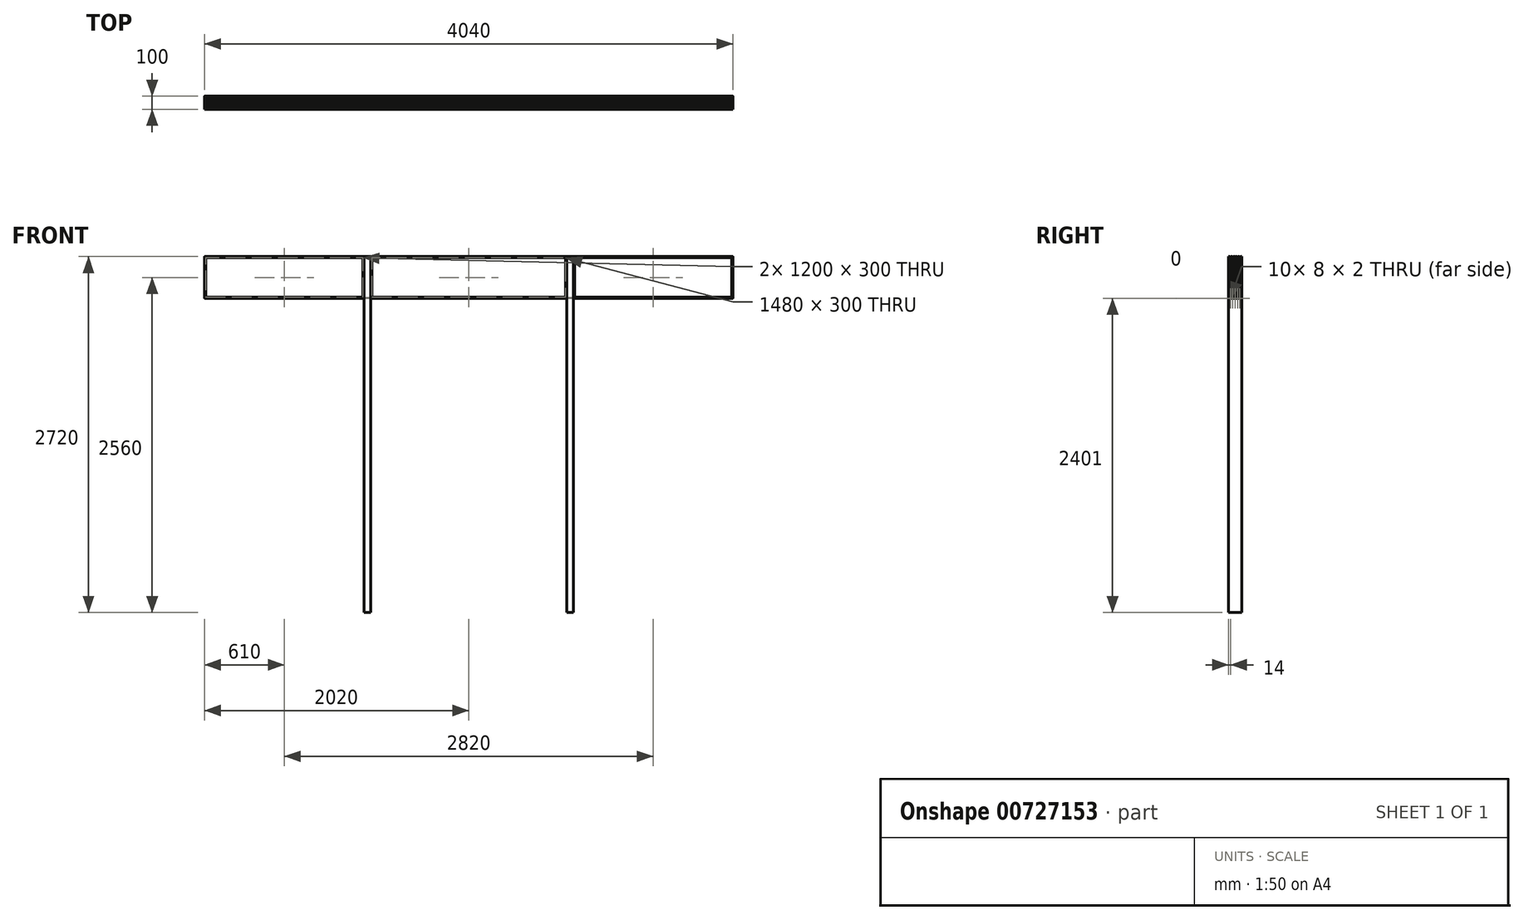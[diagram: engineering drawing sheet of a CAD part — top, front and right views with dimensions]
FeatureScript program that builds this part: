
annotation { "Feature Type Name" : "Feature", "Feature Type Description" : "" }
export const myFeature = defineFeature(function(context is Context, id is Id, definition is map)
    precondition{}
    {
        {
            var Q0;
            Q0=qCreatedBy(makeId("Front.planeOp"),FACE);
            var sketch = newSketch(context, id + "F0", { "sketchPlane" : qUnion([Q0])});
            skLineSegment(sketch, "E0.bottom", {"start": v(-800, 0) * mm, "end": v(-750, 0) * mm});
            skLineSegment(sketch, "E0.top", {"start": v(-800, -2720) * mm, "end": v(-750, -2720) * mm});
            skLineSegment(sketch, "E0.left", {"start": v(-800, 0) * mm, "end": v(-800, -2720) * mm});
            skLineSegment(sketch, "E0.right", {"start": v(-750, 0) * mm, "end": v(-750, -2720) * mm});
            skLineSegment(sketch, "E1.MirrorCS", {"start": v(800, -2720) * mm, "end": v(750, -2720) * mm});
            skLineSegment(sketch, "E2.MirrorCS", {"start": v(750, 0) * mm, "end": v(750, -2720) * mm});
            skLineSegment(sketch, "E3.MirrorCS", {"start": v(800, 0) * mm, "end": v(750, 0) * mm});
            skLineSegment(sketch, "E4.MirrorCS", {"start": v(800, 0) * mm, "end": v(800, -2720) * mm});
            skSolve(sketch);
        }
        {
            var Q0;
            Q0=qSketchRegion(id+"F0",true);
            extrude(context, id + "F1", {"entities" : qUnion([Q0]), "depth" : 100 * mm, "offsetDistance" : 25 * mm});
        }
        {
            var Q0;
            Q0=makeQuery(id+"F1.opExtrude","SWEPT_FACE",FACE,{"disambiguationData":[OSD([sQuery(id+"F0.wireOp",EDGE,"E0.bottom")])]});
            var sketch = newSketch(context, id + "F2", { "sketchPlane" : qUnion([Q0])});
            skLineSegment(sketch, "E5.bottom", {"start": v(-800, -100) * mm, "end": v(-2020, -100) * mm});
            skLineSegment(sketch, "E5.top", {"start": v(-800, 0) * mm, "end": v(-2020, 0) * mm});
            skLineSegment(sketch, "E5.left", {"start": v(-800, -100) * mm, "end": v(-800, 0) * mm});
            skLineSegment(sketch, "E5.right", {"start": v(-2020, -100) * mm, "end": v(-2020, 0) * mm});
            skLineSegment(sketch, "E6.bottom", {"start": v(-750, -100) * mm, "end": v(750, -100) * mm});
            skLineSegment(sketch, "E6.top", {"start": v(-750, 0) * mm, "end": v(750, 0) * mm});
            skLineSegment(sketch, "E6.left", {"start": v(-750, -100) * mm, "end": v(-750, 0) * mm});
            skLineSegment(sketch, "E6.right", {"start": v(750, -100) * mm, "end": v(750, 0) * mm});
            skLineSegment(sketch, "E7.bottom", {"start": v(800, -100) * mm, "end": v(2020, -100) * mm});
            skLineSegment(sketch, "E7.top", {"start": v(800, 0) * mm, "end": v(2020, 0) * mm});
            skLineSegment(sketch, "E7.left", {"start": v(800, -100) * mm, "end": v(800, 0) * mm});
            skLineSegment(sketch, "E7.right", {"start": v(2020, -100) * mm, "end": v(2020, 0) * mm});
            skSolve(sketch);
        }
        {
            var Q0;
            Q0=qSketchRegion(id+"F2",true);
            extrude(context, id + "F3", {"entities" : qUnion([Q0]), "oppositeDirection" : true, "depth" : 320 * mm, "offsetDistance" : 25 * mm});
        }
        {
            var Q0;
            Q0=makeQuery(id+"F3.opExtrude","SWEPT_FACE",FACE,{"disambiguationData":[OSD([sQuery(id+"F2.wireOp",EDGE,"E6.bottom")])]});
            var sketch = newSketch(context, id + "F4", { "sketchPlane" : qUnion([Q0])});
            skLineSegment(sketch, "E8.0", {"start": v(-810, -10) * mm, "end": v(-2010, -10) * mm});
            skLineSegment(sketch, "E8.1", {"start": v(-810, -310) * mm, "end": v(-810, -10) * mm});
            skLineSegment(sketch, "E8.2", {"start": v(-2010, -310) * mm, "end": v(-810, -310) * mm});
            skLineSegment(sketch, "E8.3", {"start": v(-2010, -10) * mm, "end": v(-2010, -310) * mm});
            skLineSegment(sketch, "E9.0", {"start": v(740, -10) * mm, "end": v(-740, -10) * mm});
            skLineSegment(sketch, "E9.1", {"start": v(740, -310) * mm, "end": v(740, -10) * mm});
            skLineSegment(sketch, "E9.2", {"start": v(-740, -310) * mm, "end": v(740, -310) * mm});
            skLineSegment(sketch, "E9.3", {"start": v(-740, -10) * mm, "end": v(-740, -310) * mm});
            skLineSegment(sketch, "E10.0", {"start": v(2010, -10) * mm, "end": v(810, -10) * mm});
            skLineSegment(sketch, "E10.1", {"start": v(2010, -310) * mm, "end": v(2010, -10) * mm});
            skLineSegment(sketch, "E10.2", {"start": v(810, -310) * mm, "end": v(2010, -310) * mm});
            skLineSegment(sketch, "E10.3", {"start": v(810, -10) * mm, "end": v(810, -310) * mm});
            skSolve(sketch);
        }
        {
            var Q0;
            Q0=qSketchRegion(id+"F4",true);
            extrude(context, id + "F5", {"entities" : qUnion([Q0]), "operationType" : NewBodyOperationType.REMOVE, "endBound" : BoundingType.THROUGH_ALL, "oppositeDirection" : true, "depth" : 25 * mm, "offsetDistance" : 25 * mm});
        }
        {
            var Q0;
            Q0=makeQuery(id+"F3.opExtrude","SWEPT_FACE",FACE,{"disambiguationData":[OSD([sQuery(id+"F2.wireOp",EDGE,"E5.right")])]});
            var sketch = newSketch(context, id + "F6", { "sketchPlane" : qUnion([Q0])});
            skLineSegment(sketch, "E11", {"start": v(10, 0) * mm, "end": v(10, -2) * mm});
            skLineSegment(sketch, "E12", {"start": v(10, -2) * mm, "end": v(18, -2) * mm});
            skLineSegment(sketch, "E13", {"start": v(18, -2) * mm, "end": v(18, 0) * mm});
            skLineSegment(sketch, "E14.1.0.0", {"start": v(36, -2) * mm, "end": v(36, 0) * mm});
            skLineSegment(sketch, "E14.1.0.1", {"start": v(28, -2) * mm, "end": v(36, -2) * mm});
            skLineSegment(sketch, "E14.1.0.2", {"start": v(28, 0) * mm, "end": v(28, -2) * mm});
            skLineSegment(sketch, "E14.2.0.0", {"start": v(54, -2) * mm, "end": v(54, 0) * mm});
            skLineSegment(sketch, "E14.2.0.1", {"start": v(46, -2) * mm, "end": v(54, -2) * mm});
            skLineSegment(sketch, "E14.2.0.2", {"start": v(46, 0) * mm, "end": v(46, -2) * mm});
            skLineSegment(sketch, "E14.3.0.0", {"start": v(72, -2) * mm, "end": v(72, 0) * mm});
            skLineSegment(sketch, "E14.3.0.1", {"start": v(64, -2) * mm, "end": v(72, -2) * mm});
            skLineSegment(sketch, "E14.3.0.2", {"start": v(64, 0) * mm, "end": v(64, -2) * mm});
            skLineSegment(sketch, "E14.4.0.0", {"start": v(90, -2) * mm, "end": v(90, 0) * mm});
            skLineSegment(sketch, "E14.4.0.1", {"start": v(82, -2) * mm, "end": v(90, -2) * mm});
            skLineSegment(sketch, "E14.4.0.2", {"start": v(82, 0) * mm, "end": v(82, -2) * mm});
            skLineSegment(sketch, "E14.direction1", {"start": v(10, -2) * mm, "end": v(28, -2) * mm, "construction": true});
            skLineSegment(sketch, "E15", {"start": v(10, 0) * mm, "end": v(18, 0) * mm});
            skLineSegment(sketch, "E16", {"start": v(28, 0) * mm, "end": v(36, 0) * mm});
            skLineSegment(sketch, "E17", {"start": v(46, 0) * mm, "end": v(54, 0) * mm});
            skLineSegment(sketch, "E18", {"start": v(64, 0) * mm, "end": v(72, 0) * mm});
            skLineSegment(sketch, "E19", {"start": v(82, 0) * mm, "end": v(90, 0) * mm});
            skLineSegment(sketch, "E20", {"start": v(100, -160) * mm, "end": v(0, -160) * mm, "construction": true});
            skLineSegment(sketch, "E21.MirrorCS", {"start": v(90, -318) * mm, "end": v(90, -320) * mm});
            skLineSegment(sketch, "E22.MirrorCS", {"start": v(64, -320) * mm, "end": v(64, -318) * mm});
            skLineSegment(sketch, "E23.MirrorCS", {"start": v(10, -320) * mm, "end": v(10, -318) * mm});
            skLineSegment(sketch, "E24.MirrorCS", {"start": v(18, -318) * mm, "end": v(18, -320) * mm});
            skLineSegment(sketch, "E25.MirrorCS", {"start": v(36, -318) * mm, "end": v(36, -320) * mm});
            skLineSegment(sketch, "E26.MirrorCS", {"start": v(28, -320) * mm, "end": v(28, -318) * mm});
            skLineSegment(sketch, "E27.MirrorCS", {"start": v(54, -318) * mm, "end": v(54, -320) * mm});
            skLineSegment(sketch, "E28.MirrorCS", {"start": v(46, -320) * mm, "end": v(46, -318) * mm});
            skLineSegment(sketch, "E29.MirrorCS", {"start": v(72, -318) * mm, "end": v(72, -320) * mm});
            skLineSegment(sketch, "E30.MirrorCS", {"start": v(82, -320) * mm, "end": v(82, -318) * mm});
            skLineSegment(sketch, "E31.MirrorCS", {"start": v(10, -320) * mm, "end": v(18, -320) * mm});
            skLineSegment(sketch, "E32.MirrorCS", {"start": v(10, -318) * mm, "end": v(18, -318) * mm});
            skLineSegment(sketch, "E33.MirrorCS", {"start": v(64, -318) * mm, "end": v(72, -318) * mm});
            skLineSegment(sketch, "E34.MirrorCS", {"start": v(64, -320) * mm, "end": v(72, -320) * mm});
            skLineSegment(sketch, "E35.MirrorCS", {"start": v(82, -320) * mm, "end": v(90, -320) * mm});
            skLineSegment(sketch, "E36.MirrorCS", {"start": v(28, -320) * mm, "end": v(36, -320) * mm});
            skLineSegment(sketch, "E37.MirrorCS", {"start": v(82, -318) * mm, "end": v(90, -318) * mm});
            skLineSegment(sketch, "E38.MirrorCS", {"start": v(10, -318) * mm, "end": v(28, -318) * mm, "construction": true});
            skLineSegment(sketch, "E39.MirrorCS", {"start": v(46, -320) * mm, "end": v(54, -320) * mm});
            skLineSegment(sketch, "E40.MirrorCS", {"start": v(28, -318) * mm, "end": v(36, -318) * mm});
            skLineSegment(sketch, "E41.MirrorCS", {"start": v(46, -318) * mm, "end": v(54, -318) * mm});
            skSolve(sketch);
        }
        {
            var Q0;
            Q0=qSketchRegion(id+"F6",true);
            extrude(context, id + "F7", {"entities" : qUnion([Q0]), "operationType" : NewBodyOperationType.REMOVE, "endBound" : BoundingType.THROUGH_ALL, "oppositeDirection" : true, "depth" : 25 * mm, "offsetDistance" : 25 * mm});
        }
        {
            var Q0;
            {var subQ0=sQuery(id+"F2.wireOp",EDGE,"E5.top");var subQ1=sQuery(id+"F2.wireOp",EDGE,"E5.left");var subQ2=sQuery(id+"F2.wireOp",EDGE,"E5.right");Q0=makeQuery(id+"F7.boolean.opBoolean","SPLIT",FACE,{"disambiguationData":[TD([makeQuery(id+"F3.opExtrude","SWEPT_FACE",FACE,{"disambiguationData":[OSD([subQ0])]})])],"derivedFrom":makeQuery(id+"F3.opExtrude","CAP_FACE",FACE,{"disambiguationData":[OSD([sQuery(id+"F2.wireOp",EDGE,"E5.bottom"),subQ0,subQ1,subQ2])],"isStart":true})});}
            var sketch = newSketch(context, id + "F8", { "sketchPlane" : qUnion([Q0])});
            skLineSegment(sketch, "E42.bottom", {"start": v(-2018, -90) * mm, "end": v(-2020, -90) * mm});
            skLineSegment(sketch, "E42.top", {"start": v(-2018, -82) * mm, "end": v(-2020, -82) * mm});
            skLineSegment(sketch, "E42.left", {"start": v(-2018, -90) * mm, "end": v(-2018, -82) * mm});
            skLineSegment(sketch, "E42.right", {"start": v(-2020, -90) * mm, "end": v(-2020, -82) * mm});
            skLineSegment(sketch, "E43.0.1.0", {"start": v(-2018, -64) * mm, "end": v(-2020, -64) * mm});
            skLineSegment(sketch, "E43.0.1.1", {"start": v(-2018, -72) * mm, "end": v(-2020, -72) * mm});
            skLineSegment(sketch, "E43.0.1.2", {"start": v(-2020, -72) * mm, "end": v(-2020, -64) * mm});
            skLineSegment(sketch, "E43.0.1.3", {"start": v(-2018, -72) * mm, "end": v(-2018, -64) * mm});
            skLineSegment(sketch, "E43.0.2.0", {"start": v(-2018, -46) * mm, "end": v(-2020, -46) * mm});
            skLineSegment(sketch, "E43.0.2.1", {"start": v(-2018, -54) * mm, "end": v(-2020, -54) * mm});
            skLineSegment(sketch, "E43.0.2.2", {"start": v(-2020, -54) * mm, "end": v(-2020, -46) * mm});
            skLineSegment(sketch, "E43.0.2.3", {"start": v(-2018, -54) * mm, "end": v(-2018, -46) * mm});
            skLineSegment(sketch, "E43.0.3.0", {"start": v(-2018, -28) * mm, "end": v(-2020, -28) * mm});
            skLineSegment(sketch, "E43.0.3.1", {"start": v(-2018, -36) * mm, "end": v(-2020, -36) * mm});
            skLineSegment(sketch, "E43.0.3.2", {"start": v(-2020, -36) * mm, "end": v(-2020, -28) * mm});
            skLineSegment(sketch, "E43.0.3.3", {"start": v(-2018, -36) * mm, "end": v(-2018, -28) * mm});
            skLineSegment(sketch, "E43.0.4.0", {"start": v(-2018, -10) * mm, "end": v(-2020, -10) * mm});
            skLineSegment(sketch, "E43.0.4.1", {"start": v(-2018, -18) * mm, "end": v(-2020, -18) * mm});
            skLineSegment(sketch, "E43.0.4.2", {"start": v(-2020, -18) * mm, "end": v(-2020, -10) * mm});
            skLineSegment(sketch, "E43.0.4.3", {"start": v(-2018, -18) * mm, "end": v(-2018, -10) * mm});
            skLineSegment(sketch, "E43.direction1", {"start": v(-2770, -90) * mm, "end": v(-2020, -90) * mm, "construction": true});
            skLineSegment(sketch, "E43.direction2", {"start": v(-2020, -90) * mm, "end": v(-2020, -72) * mm, "construction": true});
            skPoint(sketch, "E44.0", {"position": v(0, -10) * mm});
            skLineSegment(sketch, "E45.MirrorCS", {"start": v(2018, -64) * mm, "end": v(2020, -64) * mm});
            skLineSegment(sketch, "E46.MirrorCS", {"start": v(2018, -36) * mm, "end": v(2020, -36) * mm});
            skLineSegment(sketch, "E47.MirrorCS", {"start": v(2018, -90) * mm, "end": v(2020, -90) * mm});
            skLineSegment(sketch, "E48.MirrorCS", {"start": v(2018, -82) * mm, "end": v(2020, -82) * mm});
            skLineSegment(sketch, "E49.MirrorCS", {"start": v(2018, -72) * mm, "end": v(2020, -72) * mm});
            skLineSegment(sketch, "E50.MirrorCS", {"start": v(2018, -46) * mm, "end": v(2020, -46) * mm});
            skLineSegment(sketch, "E51.MirrorCS", {"start": v(2018, -54) * mm, "end": v(2020, -54) * mm});
            skLineSegment(sketch, "E52.MirrorCS", {"start": v(2020, -36) * mm, "end": v(2020, -28) * mm});
            skLineSegment(sketch, "E53.MirrorCS", {"start": v(2018, -90) * mm, "end": v(2018, -82) * mm});
            skLineSegment(sketch, "E54.MirrorCS", {"start": v(2020, -72) * mm, "end": v(2020, -64) * mm});
            skLineSegment(sketch, "E55.MirrorCS", {"start": v(2020, -54) * mm, "end": v(2020, -46) * mm});
            skLineSegment(sketch, "E56.MirrorCS", {"start": v(2018, -36) * mm, "end": v(2018, -28) * mm});
            skLineSegment(sketch, "E57.MirrorCS", {"start": v(2020, -90) * mm, "end": v(2020, -82) * mm});
            skLineSegment(sketch, "E58.MirrorCS", {"start": v(2018, -72) * mm, "end": v(2018, -64) * mm});
            skLineSegment(sketch, "E59.MirrorCS", {"start": v(2018, -54) * mm, "end": v(2018, -46) * mm});
            skLineSegment(sketch, "E60.MirrorCS", {"start": v(2018, -28) * mm, "end": v(2020, -28) * mm});
            skLineSegment(sketch, "E61.MirrorCS", {"start": v(2020, -90) * mm, "end": v(2020, -72) * mm, "construction": true});
            skLineSegment(sketch, "E62.MirrorCS", {"start": v(2770, -90) * mm, "end": v(2020, -90) * mm, "construction": true});
            skLineSegment(sketch, "E63.MirrorCS", {"start": v(2018, -18) * mm, "end": v(2020, -18) * mm});
            skLineSegment(sketch, "E64.MirrorCS", {"start": v(2020, -18) * mm, "end": v(2020, -10) * mm});
            skLineSegment(sketch, "E65.MirrorCS", {"start": v(2018, -18) * mm, "end": v(2018, -10) * mm});
            skLineSegment(sketch, "E66.MirrorCS", {"start": v(2018, -10) * mm, "end": v(2020, -10) * mm});
            skSolve(sketch);
        }
        {
            var Q0;
            Q0=qSketchRegion(id+"F8",true);
            extrude(context, id + "F9", {"entities" : qUnion([Q0]), "operationType" : NewBodyOperationType.REMOVE, "endBound" : BoundingType.THROUGH_ALL, "oppositeDirection" : true, "depth" : 25 * mm, "offsetDistance" : 25 * mm});
        }
        {
            var Q0;
            Q0=makeQuery(id+"F3.opExtrude","SWEPT_FACE",FACE,{"disambiguationData":[OSD([sQuery(id+"F2.wireOp",EDGE,"E7.top")])]});
            cPlane(context, id + "F10", {"entities" : qUnion([Q0]), "cplaneType" : CPlaneType.OFFSET, "offset" : 1 * mm, "oppositeDirection" : true, "width" : 150 * mm, "height" : 150 * mm});
        }
        {
            var Q0;
            Q0=qCreatedBy(id+"F10.planeOp",FACE);
            var sketch = newSketch(context, id + "F11", { "sketchPlane" : qUnion([Q0])});
            skLineSegment(sketch, "E67.0", {"start": v(740, -10) * mm, "end": v(740, -310) * mm});
            skLineSegment(sketch, "E67.1", {"start": v(-740, -10) * mm, "end": v(740, -10) * mm});
            skLineSegment(sketch, "E67.2", {"start": v(740, -310) * mm, "end": v(-740, -310) * mm});
            skLineSegment(sketch, "E67.3", {"start": v(-740, -310) * mm, "end": v(-740, -10) * mm});
            skLineSegment(sketch, "E67.4", {"start": v(-810, -10) * mm, "end": v(-810, -310) * mm});
            skLineSegment(sketch, "E67.5", {"start": v(-810, -310) * mm, "end": v(-2010, -310) * mm});
            skLineSegment(sketch, "E67.6", {"start": v(-2010, -10) * mm, "end": v(-810, -10) * mm});
            skLineSegment(sketch, "E67.7", {"start": v(-2010, -310) * mm, "end": v(-2010, -10) * mm});
            skLineSegment(sketch, "E67.8", {"start": v(810, -10) * mm, "end": v(810, -310) * mm});
            skLineSegment(sketch, "E67.9", {"start": v(810, -310) * mm, "end": v(2010, -310) * mm});
            skLineSegment(sketch, "E67.10", {"start": v(2010, -10) * mm, "end": v(810, -10) * mm});
            skLineSegment(sketch, "E67.11", {"start": v(2010, -310) * mm, "end": v(2010, -10) * mm});
            skSolve(sketch);
        }
        {
            var Q0;
            Q0=qSketchRegion(id+"F11",true);
            var Q1;
            Q1=makeQuery(id+"F3.opExtrude","SWEPT_FACE",FACE,{"disambiguationData":[OSD([sQuery(id+"F2.wireOp",EDGE,"E5.bottom")])]});
            extrude(context, id + "F12", {"entities" : qUnion([Q0]), "endBound" : BoundingType.UP_TO_SURFACE, "oppositeDirection" : true, "depth" : 25 * mm, "endBoundEntityFace" : qUnion([Q1]), "hasOffset" : true, "offsetDistance" : 1 * mm});
        }
        {
            var Q0;
            {var subQ0=sQuery(id+"F2.wireOp",EDGE,"E7.right");var subQ1=sQuery(id+"F2.wireOp",EDGE,"E7.top");Q0=makeQuery(id+"F7.boolean.opBoolean","SPLIT",EDGE,{"disambiguationData":[TD([makeQuery(id+"F3.opExtrude","SWEPT_FACE",FACE,{"disambiguationData":[OSD([subQ1])]})])],"derivedFrom":makeQuery(id+"F3.opExtrude","CAP_EDGE",EDGE,{"disambiguationData":[OSD([subQ0])],"isStart":true})});}
            var Q1;
            {var subQ0=sQuery(id+"F2.wireOp",EDGE,"E7.right");Q1=makeQuery(id+"F7.boolean.opBoolean","SPLIT",EDGE,{"disambiguationData":[TD([makeQuery(id+"F7.opExtrude","SWEPT_FACE",FACE,{"disambiguationData":[OSD([sQuery(id+"F6.wireOp",EDGE,"E13")])]})])],"derivedFrom":makeQuery(id+"F3.opExtrude","CAP_EDGE",EDGE,{"disambiguationData":[OSD([subQ0])],"isStart":true})});}
            var Q2;
            {var subQ0=sQuery(id+"F2.wireOp",EDGE,"E7.right");Q2=makeQuery(id+"F7.boolean.opBoolean","SPLIT",EDGE,{"disambiguationData":[TD([makeQuery(id+"F7.opExtrude","SWEPT_FACE",FACE,{"disambiguationData":[OSD([sQuery(id+"F6.wireOp",EDGE,"E14.1.0.0")])]})])],"derivedFrom":makeQuery(id+"F3.opExtrude","CAP_EDGE",EDGE,{"disambiguationData":[OSD([subQ0])],"isStart":true})});}
            var Q3;
            {var subQ0=sQuery(id+"F2.wireOp",EDGE,"E7.right");Q3=makeQuery(id+"F7.boolean.opBoolean","SPLIT",EDGE,{"disambiguationData":[TD([makeQuery(id+"F7.opExtrude","SWEPT_FACE",FACE,{"disambiguationData":[OSD([sQuery(id+"F6.wireOp",EDGE,"E14.2.0.0")])]})])],"derivedFrom":makeQuery(id+"F3.opExtrude","CAP_EDGE",EDGE,{"disambiguationData":[OSD([subQ0])],"isStart":true})});}
            var Q4;
            {var subQ0=sQuery(id+"F2.wireOp",EDGE,"E7.right");Q4=makeQuery(id+"F7.boolean.opBoolean","SPLIT",EDGE,{"disambiguationData":[TD([makeQuery(id+"F7.opExtrude","SWEPT_FACE",FACE,{"disambiguationData":[OSD([sQuery(id+"F6.wireOp",EDGE,"E14.3.0.0")])]})])],"derivedFrom":makeQuery(id+"F3.opExtrude","CAP_EDGE",EDGE,{"disambiguationData":[OSD([subQ0])],"isStart":true})});}
            var Q5;
            {var subQ0=sQuery(id+"F2.wireOp",EDGE,"E7.bottom");var subQ1=sQuery(id+"F2.wireOp",EDGE,"E7.right");Q5=makeQuery(id+"F7.boolean.opBoolean","SPLIT",EDGE,{"disambiguationData":[TD([makeQuery(id+"F3.opExtrude","SWEPT_FACE",FACE,{"disambiguationData":[OSD([subQ0])]})])],"derivedFrom":makeQuery(id+"F3.opExtrude","CAP_EDGE",EDGE,{"disambiguationData":[OSD([subQ1])],"isStart":true})});}
            var Q6;
            Q6=makeQuery(id+"F9.boolean.opBoolean","INTERSECT",EDGE,{"derivedFrom":[makeQuery(id+"F7.boolean.opBoolean","COPY",FACE,{"disambiguationData":[TD([makeQuery(id+"F3.opExtrude","SWEPT_FACE",FACE,{"disambiguationData":[OSD([sQuery(id+"F2.wireOp",EDGE,"E7.left")])]})])],"derivedFrom":makeQuery(id+"F7.opExtrude","SWEPT_FACE",FACE,{"disambiguationData":[OSD([sQuery(id+"F6.wireOp",EDGE,"E14.4.0.1")])]})}),makeQuery(id+"F9.opExtrude","SWEPT_FACE",FACE,{"disambiguationData":[OSD([sQuery(id+"F8.wireOp",EDGE,"E53.MirrorCS")])]})]});
            var Q7;
            Q7=makeQuery(id+"F9.boolean.opBoolean","INTERSECT",EDGE,{"derivedFrom":[makeQuery(id+"F7.boolean.opBoolean","COPY",FACE,{"disambiguationData":[TD([makeQuery(id+"F3.opExtrude","SWEPT_FACE",FACE,{"disambiguationData":[OSD([sQuery(id+"F2.wireOp",EDGE,"E7.left")])]})])],"derivedFrom":makeQuery(id+"F7.opExtrude","SWEPT_FACE",FACE,{"disambiguationData":[OSD([sQuery(id+"F6.wireOp",EDGE,"E14.3.0.1")])]})}),makeQuery(id+"F9.opExtrude","SWEPT_FACE",FACE,{"disambiguationData":[OSD([sQuery(id+"F8.wireOp",EDGE,"E58.MirrorCS")])]})]});
            var Q8;
            Q8=makeQuery(id+"F9.boolean.opBoolean","INTERSECT",EDGE,{"derivedFrom":[makeQuery(id+"F7.boolean.opBoolean","COPY",FACE,{"disambiguationData":[TD([makeQuery(id+"F3.opExtrude","SWEPT_FACE",FACE,{"disambiguationData":[OSD([sQuery(id+"F2.wireOp",EDGE,"E7.left")])]})])],"derivedFrom":makeQuery(id+"F7.opExtrude","SWEPT_FACE",FACE,{"disambiguationData":[OSD([sQuery(id+"F6.wireOp",EDGE,"E14.2.0.1")])]})}),makeQuery(id+"F9.opExtrude","SWEPT_FACE",FACE,{"disambiguationData":[OSD([sQuery(id+"F8.wireOp",EDGE,"E59.MirrorCS")])]})]});
            var Q9;
            Q9=makeQuery(id+"F9.boolean.opBoolean","INTERSECT",EDGE,{"derivedFrom":[makeQuery(id+"F7.boolean.opBoolean","COPY",FACE,{"disambiguationData":[TD([makeQuery(id+"F3.opExtrude","SWEPT_FACE",FACE,{"disambiguationData":[OSD([sQuery(id+"F2.wireOp",EDGE,"E7.left")])]})])],"derivedFrom":makeQuery(id+"F7.opExtrude","SWEPT_FACE",FACE,{"disambiguationData":[OSD([sQuery(id+"F6.wireOp",EDGE,"E14.1.0.1")])]})}),makeQuery(id+"F9.opExtrude","SWEPT_FACE",FACE,{"disambiguationData":[OSD([sQuery(id+"F8.wireOp",EDGE,"E56.MirrorCS")])]})]});
            var Q10;
            Q10=makeQuery(id+"F9.boolean.opBoolean","INTERSECT",EDGE,{"derivedFrom":[makeQuery(id+"F7.boolean.opBoolean","COPY",FACE,{"disambiguationData":[TD([makeQuery(id+"F3.opExtrude","SWEPT_FACE",FACE,{"disambiguationData":[OSD([sQuery(id+"F2.wireOp",EDGE,"E7.left")])]})])],"derivedFrom":makeQuery(id+"F7.opExtrude","SWEPT_FACE",FACE,{"disambiguationData":[OSD([sQuery(id+"F6.wireOp",EDGE,"E12")])]})}),makeQuery(id+"F9.opExtrude","SWEPT_FACE",FACE,{"disambiguationData":[OSD([sQuery(id+"F8.wireOp",EDGE,"E65.MirrorCS")])]})]});
            var Q11;
            {var subQ0=sQuery(id+"F2.wireOp",EDGE,"E7.left");var subQ1=sQuery(id+"F2.wireOp",EDGE,"E7.top");Q11=makeQuery(id+"F7.boolean.opBoolean","SPLIT",EDGE,{"disambiguationData":[TD([makeQuery(id+"F3.opExtrude","SWEPT_FACE",FACE,{"disambiguationData":[OSD([subQ1])]})])],"derivedFrom":makeQuery(id+"F3.opExtrude","CAP_EDGE",EDGE,{"disambiguationData":[OSD([subQ0])],"isStart":true})});}
            var Q12;
            {var subQ0=sQuery(id+"F2.wireOp",EDGE,"E7.left");Q12=makeQuery(id+"F7.boolean.opBoolean","SPLIT",EDGE,{"disambiguationData":[TD([makeQuery(id+"F7.opExtrude","SWEPT_FACE",FACE,{"disambiguationData":[OSD([sQuery(id+"F6.wireOp",EDGE,"E13")])]})])],"derivedFrom":makeQuery(id+"F3.opExtrude","CAP_EDGE",EDGE,{"disambiguationData":[OSD([subQ0])],"isStart":true})});}
            var Q13;
            {var subQ0=sQuery(id+"F2.wireOp",EDGE,"E7.left");Q13=makeQuery(id+"F7.boolean.opBoolean","SPLIT",EDGE,{"disambiguationData":[TD([makeQuery(id+"F7.opExtrude","SWEPT_FACE",FACE,{"disambiguationData":[OSD([sQuery(id+"F6.wireOp",EDGE,"E14.1.0.0")])]})])],"derivedFrom":makeQuery(id+"F3.opExtrude","CAP_EDGE",EDGE,{"disambiguationData":[OSD([subQ0])],"isStart":true})});}
            var Q14;
            {var subQ0=sQuery(id+"F2.wireOp",EDGE,"E7.left");Q14=makeQuery(id+"F7.boolean.opBoolean","SPLIT",EDGE,{"disambiguationData":[TD([makeQuery(id+"F7.opExtrude","SWEPT_FACE",FACE,{"disambiguationData":[OSD([sQuery(id+"F6.wireOp",EDGE,"E14.2.0.0")])]})])],"derivedFrom":makeQuery(id+"F3.opExtrude","CAP_EDGE",EDGE,{"disambiguationData":[OSD([subQ0])],"isStart":true})});}
            var Q15;
            {var subQ0=sQuery(id+"F2.wireOp",EDGE,"E7.bottom");var subQ1=sQuery(id+"F2.wireOp",EDGE,"E7.left");Q15=makeQuery(id+"F7.boolean.opBoolean","SPLIT",EDGE,{"disambiguationData":[TD([makeQuery(id+"F3.opExtrude","SWEPT_FACE",FACE,{"disambiguationData":[OSD([subQ0])]})])],"derivedFrom":makeQuery(id+"F3.opExtrude","CAP_EDGE",EDGE,{"disambiguationData":[OSD([subQ1])],"isStart":true})});}
            var Q16;
            Q16=makeQuery(id+"F1.opExtrude","SWEPT_EDGE",EDGE,{"disambiguationData":[OSD([sQuery(id+"F0.wireOp",EDGE,"E3.MirrorCS"),sQuery(id+"F0.wireOp",EDGE,"E4.MirrorCS")])]});
            var Q17;
            {var subQ0=sQuery(id+"F2.wireOp",EDGE,"E7.left");Q17=makeQuery(id+"F7.boolean.opBoolean","SPLIT",EDGE,{"disambiguationData":[TD([makeQuery(id+"F7.opExtrude","SWEPT_FACE",FACE,{"disambiguationData":[OSD([sQuery(id+"F6.wireOp",EDGE,"E14.3.0.0")])]})])],"derivedFrom":makeQuery(id+"F3.opExtrude","CAP_EDGE",EDGE,{"disambiguationData":[OSD([subQ0])],"isStart":true})});}
            var Q18;
            Q18=makeQuery(id+"F7.boolean.opBoolean","INTERSECT",EDGE,{"derivedFrom":[makeQuery(id+"F3.opExtrude","SWEPT_FACE",FACE,{"disambiguationData":[OSD([sQuery(id+"F2.wireOp",EDGE,"E7.left")])]}),makeQuery(id+"F7.opExtrude","SWEPT_FACE",FACE,{"disambiguationData":[OSD([sQuery(id+"F6.wireOp",EDGE,"E14.4.0.1")])]})]});
            var Q19;
            Q19=makeQuery(id+"F7.boolean.opBoolean","INTERSECT",EDGE,{"derivedFrom":[makeQuery(id+"F3.opExtrude","SWEPT_FACE",FACE,{"disambiguationData":[OSD([sQuery(id+"F2.wireOp",EDGE,"E7.left")])]}),makeQuery(id+"F7.opExtrude","SWEPT_FACE",FACE,{"disambiguationData":[OSD([sQuery(id+"F6.wireOp",EDGE,"E14.3.0.1")])]})]});
            var Q20;
            Q20=makeQuery(id+"F7.boolean.opBoolean","INTERSECT",EDGE,{"derivedFrom":[makeQuery(id+"F3.opExtrude","SWEPT_FACE",FACE,{"disambiguationData":[OSD([sQuery(id+"F2.wireOp",EDGE,"E7.left")])]}),makeQuery(id+"F7.opExtrude","SWEPT_FACE",FACE,{"disambiguationData":[OSD([sQuery(id+"F6.wireOp",EDGE,"E14.2.0.1")])]})]});
            var Q21;
            Q21=makeQuery(id+"F7.boolean.opBoolean","INTERSECT",EDGE,{"derivedFrom":[makeQuery(id+"F3.opExtrude","SWEPT_FACE",FACE,{"disambiguationData":[OSD([sQuery(id+"F2.wireOp",EDGE,"E7.left")])]}),makeQuery(id+"F7.opExtrude","SWEPT_FACE",FACE,{"disambiguationData":[OSD([sQuery(id+"F6.wireOp",EDGE,"E14.1.0.1")])]})]});
            var Q22;
            Q22=makeQuery(id+"F7.boolean.opBoolean","INTERSECT",EDGE,{"derivedFrom":[makeQuery(id+"F3.opExtrude","SWEPT_FACE",FACE,{"disambiguationData":[OSD([sQuery(id+"F2.wireOp",EDGE,"E7.left")])]}),makeQuery(id+"F7.opExtrude","SWEPT_FACE",FACE,{"disambiguationData":[OSD([sQuery(id+"F6.wireOp",EDGE,"E12")])]})]});
            var Q23;
            Q23=makeQuery(id+"F1.opExtrude","SWEPT_FACE",FACE,{"disambiguationData":[OSD([sQuery(id+"F0.wireOp",EDGE,"E3.MirrorCS")])]});
            var Q24;
            {var subQ0=sQuery(id+"F2.wireOp",EDGE,"E6.right");Q24=makeQuery(id+"F7.boolean.opBoolean","SPLIT",EDGE,{"disambiguationData":[TD([makeQuery(id+"F7.opExtrude","SWEPT_FACE",FACE,{"disambiguationData":[OSD([sQuery(id+"F6.wireOp",EDGE,"E14.1.0.0")])]})])],"derivedFrom":makeQuery(id+"F3.opExtrude","CAP_EDGE",EDGE,{"disambiguationData":[OSD([subQ0])],"isStart":true})});}
            var Q25;
            {var subQ0=sQuery(id+"F2.wireOp",EDGE,"E6.right");Q25=makeQuery(id+"F7.boolean.opBoolean","SPLIT",EDGE,{"disambiguationData":[TD([makeQuery(id+"F7.opExtrude","SWEPT_FACE",FACE,{"disambiguationData":[OSD([sQuery(id+"F6.wireOp",EDGE,"E13")])]})])],"derivedFrom":makeQuery(id+"F3.opExtrude","CAP_EDGE",EDGE,{"disambiguationData":[OSD([subQ0])],"isStart":true})});}
            var Q26;
            {var subQ0=sQuery(id+"F2.wireOp",EDGE,"E6.right");var subQ1=sQuery(id+"F2.wireOp",EDGE,"E6.top");Q26=makeQuery(id+"F7.boolean.opBoolean","SPLIT",EDGE,{"disambiguationData":[TD([makeQuery(id+"F3.opExtrude","SWEPT_FACE",FACE,{"disambiguationData":[OSD([subQ1])]})])],"derivedFrom":makeQuery(id+"F3.opExtrude","CAP_EDGE",EDGE,{"disambiguationData":[OSD([subQ0])],"isStart":true})});}
            var Q27;
            {var subQ0=sQuery(id+"F2.wireOp",EDGE,"E6.right");Q27=makeQuery(id+"F7.boolean.opBoolean","SPLIT",EDGE,{"disambiguationData":[TD([makeQuery(id+"F7.opExtrude","SWEPT_FACE",FACE,{"disambiguationData":[OSD([sQuery(id+"F6.wireOp",EDGE,"E14.2.0.0")])]})])],"derivedFrom":makeQuery(id+"F3.opExtrude","CAP_EDGE",EDGE,{"disambiguationData":[OSD([subQ0])],"isStart":true})});}
            var Q28;
            {var subQ0=sQuery(id+"F2.wireOp",EDGE,"E6.right");Q28=makeQuery(id+"F7.boolean.opBoolean","SPLIT",EDGE,{"disambiguationData":[TD([makeQuery(id+"F7.opExtrude","SWEPT_FACE",FACE,{"disambiguationData":[OSD([sQuery(id+"F6.wireOp",EDGE,"E14.3.0.0")])]})])],"derivedFrom":makeQuery(id+"F3.opExtrude","CAP_EDGE",EDGE,{"disambiguationData":[OSD([subQ0])],"isStart":true})});}
            var Q29;
            {var subQ0=sQuery(id+"F2.wireOp",EDGE,"E6.bottom");var subQ1=sQuery(id+"F2.wireOp",EDGE,"E6.right");Q29=makeQuery(id+"F7.boolean.opBoolean","SPLIT",EDGE,{"disambiguationData":[TD([makeQuery(id+"F3.opExtrude","SWEPT_FACE",FACE,{"disambiguationData":[OSD([subQ0])]})])],"derivedFrom":makeQuery(id+"F3.opExtrude","CAP_EDGE",EDGE,{"disambiguationData":[OSD([subQ1])],"isStart":true})});}
            var Q30;
            Q30=makeQuery(id+"F7.boolean.opBoolean","INTERSECT",EDGE,{"derivedFrom":[makeQuery(id+"F3.opExtrude","SWEPT_FACE",FACE,{"disambiguationData":[OSD([sQuery(id+"F2.wireOp",EDGE,"E6.right")])]}),makeQuery(id+"F7.opExtrude","SWEPT_FACE",FACE,{"disambiguationData":[OSD([sQuery(id+"F6.wireOp",EDGE,"E14.4.0.1")])]})]});
            var Q31;
            Q31=makeQuery(id+"F7.boolean.opBoolean","INTERSECT",EDGE,{"derivedFrom":[makeQuery(id+"F3.opExtrude","SWEPT_FACE",FACE,{"disambiguationData":[OSD([sQuery(id+"F2.wireOp",EDGE,"E6.right")])]}),makeQuery(id+"F7.opExtrude","SWEPT_FACE",FACE,{"disambiguationData":[OSD([sQuery(id+"F6.wireOp",EDGE,"E14.3.0.1")])]})]});
            var Q32;
            Q32=makeQuery(id+"F7.boolean.opBoolean","INTERSECT",EDGE,{"derivedFrom":[makeQuery(id+"F3.opExtrude","SWEPT_FACE",FACE,{"disambiguationData":[OSD([sQuery(id+"F2.wireOp",EDGE,"E6.right")])]}),makeQuery(id+"F7.opExtrude","SWEPT_FACE",FACE,{"disambiguationData":[OSD([sQuery(id+"F6.wireOp",EDGE,"E14.2.0.1")])]})]});
            var Q33;
            Q33=makeQuery(id+"F7.boolean.opBoolean","INTERSECT",EDGE,{"derivedFrom":[makeQuery(id+"F3.opExtrude","SWEPT_FACE",FACE,{"disambiguationData":[OSD([sQuery(id+"F2.wireOp",EDGE,"E6.right")])]}),makeQuery(id+"F7.opExtrude","SWEPT_FACE",FACE,{"disambiguationData":[OSD([sQuery(id+"F6.wireOp",EDGE,"E14.1.0.1")])]})]});
            var Q34;
            Q34=makeQuery(id+"F7.boolean.opBoolean","INTERSECT",EDGE,{"derivedFrom":[makeQuery(id+"F3.opExtrude","SWEPT_FACE",FACE,{"disambiguationData":[OSD([sQuery(id+"F2.wireOp",EDGE,"E6.right")])]}),makeQuery(id+"F7.opExtrude","SWEPT_FACE",FACE,{"disambiguationData":[OSD([sQuery(id+"F6.wireOp",EDGE,"E12")])]})]});
            var Q35;
            {var subQ0=sQuery(id+"F2.wireOp",EDGE,"E7.right");var subQ1=sQuery(id+"F2.wireOp",EDGE,"E7.top");Q35=makeQuery(id+"F7.boolean.opBoolean","SPLIT",EDGE,{"disambiguationData":[TD([makeQuery(id+"F3.opExtrude","SWEPT_FACE",FACE,{"disambiguationData":[OSD([subQ1])]})])],"derivedFrom":makeQuery(id+"F3.opExtrude","CAP_EDGE",EDGE,{"disambiguationData":[OSD([subQ0])],"isStart":false})});}
            var Q36;
            Q36=makeQuery(id+"F9.boolean.opBoolean","INTERSECT",EDGE,{"derivedFrom":[makeQuery(id+"F7.boolean.opBoolean","COPY",FACE,{"disambiguationData":[TD([makeQuery(id+"F3.opExtrude","SWEPT_FACE",FACE,{"disambiguationData":[OSD([sQuery(id+"F2.wireOp",EDGE,"E7.left")])]})])],"derivedFrom":makeQuery(id+"F7.opExtrude","SWEPT_FACE",FACE,{"disambiguationData":[OSD([sQuery(id+"F6.wireOp",EDGE,"E32.MirrorCS")])]})}),makeQuery(id+"F9.opExtrude","SWEPT_FACE",FACE,{"disambiguationData":[OSD([sQuery(id+"F8.wireOp",EDGE,"E65.MirrorCS")])]})]});
            var Q37;
            {var subQ0=sQuery(id+"F2.wireOp",EDGE,"E7.right");Q37=makeQuery(id+"F7.boolean.opBoolean","SPLIT",EDGE,{"disambiguationData":[TD([makeQuery(id+"F7.opExtrude","SWEPT_FACE",FACE,{"disambiguationData":[OSD([sQuery(id+"F6.wireOp",EDGE,"E24.MirrorCS")])]})])],"derivedFrom":makeQuery(id+"F3.opExtrude","CAP_EDGE",EDGE,{"disambiguationData":[OSD([subQ0])],"isStart":false})});}
            var Q38;
            Q38=makeQuery(id+"F9.boolean.opBoolean","INTERSECT",EDGE,{"derivedFrom":[makeQuery(id+"F7.boolean.opBoolean","COPY",FACE,{"disambiguationData":[TD([makeQuery(id+"F3.opExtrude","SWEPT_FACE",FACE,{"disambiguationData":[OSD([sQuery(id+"F2.wireOp",EDGE,"E7.left")])]})])],"derivedFrom":makeQuery(id+"F7.opExtrude","SWEPT_FACE",FACE,{"disambiguationData":[OSD([sQuery(id+"F6.wireOp",EDGE,"E40.MirrorCS")])]})}),makeQuery(id+"F9.opExtrude","SWEPT_FACE",FACE,{"disambiguationData":[OSD([sQuery(id+"F8.wireOp",EDGE,"E56.MirrorCS")])]})]});
            var Q39;
            {var subQ0=sQuery(id+"F2.wireOp",EDGE,"E7.right");Q39=makeQuery(id+"F7.boolean.opBoolean","SPLIT",EDGE,{"disambiguationData":[TD([makeQuery(id+"F7.opExtrude","SWEPT_FACE",FACE,{"disambiguationData":[OSD([sQuery(id+"F6.wireOp",EDGE,"E25.MirrorCS")])]})])],"derivedFrom":makeQuery(id+"F3.opExtrude","CAP_EDGE",EDGE,{"disambiguationData":[OSD([subQ0])],"isStart":false})});}
            var Q40;
            Q40=makeQuery(id+"F9.boolean.opBoolean","INTERSECT",EDGE,{"derivedFrom":[makeQuery(id+"F7.boolean.opBoolean","COPY",FACE,{"disambiguationData":[TD([makeQuery(id+"F3.opExtrude","SWEPT_FACE",FACE,{"disambiguationData":[OSD([sQuery(id+"F2.wireOp",EDGE,"E7.left")])]})])],"derivedFrom":makeQuery(id+"F7.opExtrude","SWEPT_FACE",FACE,{"disambiguationData":[OSD([sQuery(id+"F6.wireOp",EDGE,"E41.MirrorCS")])]})}),makeQuery(id+"F9.opExtrude","SWEPT_FACE",FACE,{"disambiguationData":[OSD([sQuery(id+"F8.wireOp",EDGE,"E59.MirrorCS")])]})]});
            var Q41;
            {var subQ0=sQuery(id+"F2.wireOp",EDGE,"E7.right");Q41=makeQuery(id+"F7.boolean.opBoolean","SPLIT",EDGE,{"disambiguationData":[TD([makeQuery(id+"F7.opExtrude","SWEPT_FACE",FACE,{"disambiguationData":[OSD([sQuery(id+"F6.wireOp",EDGE,"E22.MirrorCS")])]})])],"derivedFrom":makeQuery(id+"F3.opExtrude","CAP_EDGE",EDGE,{"disambiguationData":[OSD([subQ0])],"isStart":false})});}
            var Q42;
            Q42=makeQuery(id+"F9.boolean.opBoolean","INTERSECT",EDGE,{"derivedFrom":[makeQuery(id+"F7.boolean.opBoolean","COPY",FACE,{"disambiguationData":[TD([makeQuery(id+"F3.opExtrude","SWEPT_FACE",FACE,{"disambiguationData":[OSD([sQuery(id+"F2.wireOp",EDGE,"E7.left")])]})])],"derivedFrom":makeQuery(id+"F7.opExtrude","SWEPT_FACE",FACE,{"disambiguationData":[OSD([sQuery(id+"F6.wireOp",EDGE,"E33.MirrorCS")])]})}),makeQuery(id+"F9.opExtrude","SWEPT_FACE",FACE,{"disambiguationData":[OSD([sQuery(id+"F8.wireOp",EDGE,"E58.MirrorCS")])]})]});
            var Q43;
            {var subQ0=sQuery(id+"F2.wireOp",EDGE,"E7.right");Q43=makeQuery(id+"F7.boolean.opBoolean","SPLIT",EDGE,{"disambiguationData":[TD([makeQuery(id+"F7.opExtrude","SWEPT_FACE",FACE,{"disambiguationData":[OSD([sQuery(id+"F6.wireOp",EDGE,"E29.MirrorCS")])]})])],"derivedFrom":makeQuery(id+"F3.opExtrude","CAP_EDGE",EDGE,{"disambiguationData":[OSD([subQ0])],"isStart":false})});}
            var Q44;
            Q44=makeQuery(id+"F9.boolean.opBoolean","INTERSECT",EDGE,{"derivedFrom":[makeQuery(id+"F7.boolean.opBoolean","COPY",FACE,{"disambiguationData":[TD([makeQuery(id+"F3.opExtrude","SWEPT_FACE",FACE,{"disambiguationData":[OSD([sQuery(id+"F2.wireOp",EDGE,"E7.left")])]})])],"derivedFrom":makeQuery(id+"F7.opExtrude","SWEPT_FACE",FACE,{"disambiguationData":[OSD([sQuery(id+"F6.wireOp",EDGE,"E37.MirrorCS")])]})}),makeQuery(id+"F9.opExtrude","SWEPT_FACE",FACE,{"disambiguationData":[OSD([sQuery(id+"F8.wireOp",EDGE,"E53.MirrorCS")])]})]});
            var Q45;
            {var subQ0=sQuery(id+"F2.wireOp",EDGE,"E7.bottom");var subQ1=sQuery(id+"F2.wireOp",EDGE,"E7.right");Q45=makeQuery(id+"F7.boolean.opBoolean","SPLIT",EDGE,{"disambiguationData":[TD([makeQuery(id+"F3.opExtrude","SWEPT_FACE",FACE,{"disambiguationData":[OSD([subQ0])]})])],"derivedFrom":makeQuery(id+"F3.opExtrude","CAP_EDGE",EDGE,{"disambiguationData":[OSD([subQ1])],"isStart":false})});}
            var Q46;
            {var subQ0=sQuery(id+"F2.wireOp",EDGE,"E7.left");var subQ1=sQuery(id+"F2.wireOp",EDGE,"E7.top");Q46=makeQuery(id+"F7.boolean.opBoolean","SPLIT",EDGE,{"disambiguationData":[TD([makeQuery(id+"F3.opExtrude","SWEPT_FACE",FACE,{"disambiguationData":[OSD([subQ1])]})])],"derivedFrom":makeQuery(id+"F3.opExtrude","CAP_EDGE",EDGE,{"disambiguationData":[OSD([subQ0])],"isStart":false})});}
            var Q47;
            Q47=makeQuery(id+"F7.boolean.opBoolean","INTERSECT",EDGE,{"derivedFrom":[makeQuery(id+"F3.opExtrude","SWEPT_FACE",FACE,{"disambiguationData":[OSD([sQuery(id+"F2.wireOp",EDGE,"E7.left")])]}),makeQuery(id+"F7.opExtrude","SWEPT_FACE",FACE,{"disambiguationData":[OSD([sQuery(id+"F6.wireOp",EDGE,"E32.MirrorCS")])]})]});
            var Q48;
            {var subQ0=sQuery(id+"F2.wireOp",EDGE,"E7.left");Q48=makeQuery(id+"F7.boolean.opBoolean","SPLIT",EDGE,{"disambiguationData":[TD([makeQuery(id+"F7.opExtrude","SWEPT_FACE",FACE,{"disambiguationData":[OSD([sQuery(id+"F6.wireOp",EDGE,"E24.MirrorCS")])]})])],"derivedFrom":makeQuery(id+"F3.opExtrude","CAP_EDGE",EDGE,{"disambiguationData":[OSD([subQ0])],"isStart":false})});}
            var Q49;
            Q49=makeQuery(id+"F7.boolean.opBoolean","INTERSECT",EDGE,{"derivedFrom":[makeQuery(id+"F3.opExtrude","SWEPT_FACE",FACE,{"disambiguationData":[OSD([sQuery(id+"F2.wireOp",EDGE,"E7.left")])]}),makeQuery(id+"F7.opExtrude","SWEPT_FACE",FACE,{"disambiguationData":[OSD([sQuery(id+"F6.wireOp",EDGE,"E40.MirrorCS")])]})]});
            var Q50;
            {var subQ0=sQuery(id+"F2.wireOp",EDGE,"E7.left");Q50=makeQuery(id+"F7.boolean.opBoolean","SPLIT",EDGE,{"disambiguationData":[TD([makeQuery(id+"F7.opExtrude","SWEPT_FACE",FACE,{"disambiguationData":[OSD([sQuery(id+"F6.wireOp",EDGE,"E25.MirrorCS")])]})])],"derivedFrom":makeQuery(id+"F3.opExtrude","CAP_EDGE",EDGE,{"disambiguationData":[OSD([subQ0])],"isStart":false})});}
            var Q51;
            Q51=makeQuery(id+"F7.boolean.opBoolean","INTERSECT",EDGE,{"derivedFrom":[makeQuery(id+"F3.opExtrude","SWEPT_FACE",FACE,{"disambiguationData":[OSD([sQuery(id+"F2.wireOp",EDGE,"E7.left")])]}),makeQuery(id+"F7.opExtrude","SWEPT_FACE",FACE,{"disambiguationData":[OSD([sQuery(id+"F6.wireOp",EDGE,"E41.MirrorCS")])]})]});
            var Q52;
            {var subQ0=sQuery(id+"F2.wireOp",EDGE,"E7.left");Q52=makeQuery(id+"F7.boolean.opBoolean","SPLIT",EDGE,{"disambiguationData":[TD([makeQuery(id+"F7.opExtrude","SWEPT_FACE",FACE,{"disambiguationData":[OSD([sQuery(id+"F6.wireOp",EDGE,"E22.MirrorCS")])]})])],"derivedFrom":makeQuery(id+"F3.opExtrude","CAP_EDGE",EDGE,{"disambiguationData":[OSD([subQ0])],"isStart":false})});}
            var Q53;
            Q53=makeQuery(id+"F7.boolean.opBoolean","INTERSECT",EDGE,{"derivedFrom":[makeQuery(id+"F3.opExtrude","SWEPT_FACE",FACE,{"disambiguationData":[OSD([sQuery(id+"F2.wireOp",EDGE,"E7.left")])]}),makeQuery(id+"F7.opExtrude","SWEPT_FACE",FACE,{"disambiguationData":[OSD([sQuery(id+"F6.wireOp",EDGE,"E33.MirrorCS")])]})]});
            var Q54;
            {var subQ0=sQuery(id+"F2.wireOp",EDGE,"E7.left");Q54=makeQuery(id+"F7.boolean.opBoolean","SPLIT",EDGE,{"disambiguationData":[TD([makeQuery(id+"F7.opExtrude","SWEPT_FACE",FACE,{"disambiguationData":[OSD([sQuery(id+"F6.wireOp",EDGE,"E29.MirrorCS")])]})])],"derivedFrom":makeQuery(id+"F3.opExtrude","CAP_EDGE",EDGE,{"disambiguationData":[OSD([subQ0])],"isStart":false})});}
            var Q55;
            Q55=makeQuery(id+"F7.boolean.opBoolean","INTERSECT",EDGE,{"derivedFrom":[makeQuery(id+"F3.opExtrude","SWEPT_FACE",FACE,{"disambiguationData":[OSD([sQuery(id+"F2.wireOp",EDGE,"E7.left")])]}),makeQuery(id+"F7.opExtrude","SWEPT_FACE",FACE,{"disambiguationData":[OSD([sQuery(id+"F6.wireOp",EDGE,"E37.MirrorCS")])]})]});
            var Q56;
            {var subQ0=sQuery(id+"F2.wireOp",EDGE,"E7.bottom");var subQ1=sQuery(id+"F2.wireOp",EDGE,"E7.left");Q56=makeQuery(id+"F7.boolean.opBoolean","SPLIT",EDGE,{"disambiguationData":[TD([makeQuery(id+"F3.opExtrude","SWEPT_FACE",FACE,{"disambiguationData":[OSD([subQ0])]})])],"derivedFrom":makeQuery(id+"F3.opExtrude","CAP_EDGE",EDGE,{"disambiguationData":[OSD([subQ1])],"isStart":false})});}
            var Q57;
            {var subQ0=sQuery(id+"F2.wireOp",EDGE,"E6.bottom");var subQ1=sQuery(id+"F2.wireOp",EDGE,"E6.right");Q57=makeQuery(id+"F7.boolean.opBoolean","SPLIT",EDGE,{"disambiguationData":[TD([makeQuery(id+"F3.opExtrude","SWEPT_FACE",FACE,{"disambiguationData":[OSD([subQ0])]})])],"derivedFrom":makeQuery(id+"F3.opExtrude","CAP_EDGE",EDGE,{"disambiguationData":[OSD([subQ1])],"isStart":false})});}
            var Q58;
            Q58=makeQuery(id+"F7.boolean.opBoolean","INTERSECT",EDGE,{"derivedFrom":[makeQuery(id+"F3.opExtrude","SWEPT_FACE",FACE,{"disambiguationData":[OSD([sQuery(id+"F2.wireOp",EDGE,"E6.right")])]}),makeQuery(id+"F7.opExtrude","SWEPT_FACE",FACE,{"disambiguationData":[OSD([sQuery(id+"F6.wireOp",EDGE,"E37.MirrorCS")])]})]});
            var Q59;
            {var subQ0=sQuery(id+"F2.wireOp",EDGE,"E6.right");Q59=makeQuery(id+"F7.boolean.opBoolean","SPLIT",EDGE,{"disambiguationData":[TD([makeQuery(id+"F7.opExtrude","SWEPT_FACE",FACE,{"disambiguationData":[OSD([sQuery(id+"F6.wireOp",EDGE,"E29.MirrorCS")])]})])],"derivedFrom":makeQuery(id+"F3.opExtrude","CAP_EDGE",EDGE,{"disambiguationData":[OSD([subQ0])],"isStart":false})});}
            var Q60;
            Q60=makeQuery(id+"F7.boolean.opBoolean","INTERSECT",EDGE,{"derivedFrom":[makeQuery(id+"F3.opExtrude","SWEPT_FACE",FACE,{"disambiguationData":[OSD([sQuery(id+"F2.wireOp",EDGE,"E6.right")])]}),makeQuery(id+"F7.opExtrude","SWEPT_FACE",FACE,{"disambiguationData":[OSD([sQuery(id+"F6.wireOp",EDGE,"E33.MirrorCS")])]})]});
            var Q61;
            {var subQ0=sQuery(id+"F2.wireOp",EDGE,"E6.right");Q61=makeQuery(id+"F7.boolean.opBoolean","SPLIT",EDGE,{"disambiguationData":[TD([makeQuery(id+"F7.opExtrude","SWEPT_FACE",FACE,{"disambiguationData":[OSD([sQuery(id+"F6.wireOp",EDGE,"E22.MirrorCS")])]})])],"derivedFrom":makeQuery(id+"F3.opExtrude","CAP_EDGE",EDGE,{"disambiguationData":[OSD([subQ0])],"isStart":false})});}
            var Q62;
            Q62=makeQuery(id+"F7.boolean.opBoolean","INTERSECT",EDGE,{"derivedFrom":[makeQuery(id+"F3.opExtrude","SWEPT_FACE",FACE,{"disambiguationData":[OSD([sQuery(id+"F2.wireOp",EDGE,"E6.right")])]}),makeQuery(id+"F7.opExtrude","SWEPT_FACE",FACE,{"disambiguationData":[OSD([sQuery(id+"F6.wireOp",EDGE,"E41.MirrorCS")])]})]});
            var Q63;
            {var subQ0=sQuery(id+"F2.wireOp",EDGE,"E6.right");Q63=makeQuery(id+"F7.boolean.opBoolean","SPLIT",EDGE,{"disambiguationData":[TD([makeQuery(id+"F7.opExtrude","SWEPT_FACE",FACE,{"disambiguationData":[OSD([sQuery(id+"F6.wireOp",EDGE,"E25.MirrorCS")])]})])],"derivedFrom":makeQuery(id+"F3.opExtrude","CAP_EDGE",EDGE,{"disambiguationData":[OSD([subQ0])],"isStart":false})});}
            var Q64;
            Q64=makeQuery(id+"F7.boolean.opBoolean","INTERSECT",EDGE,{"derivedFrom":[makeQuery(id+"F3.opExtrude","SWEPT_FACE",FACE,{"disambiguationData":[OSD([sQuery(id+"F2.wireOp",EDGE,"E6.right")])]}),makeQuery(id+"F7.opExtrude","SWEPT_FACE",FACE,{"disambiguationData":[OSD([sQuery(id+"F6.wireOp",EDGE,"E40.MirrorCS")])]})]});
            var Q65;
            {var subQ0=sQuery(id+"F2.wireOp",EDGE,"E6.right");Q65=makeQuery(id+"F7.boolean.opBoolean","SPLIT",EDGE,{"disambiguationData":[TD([makeQuery(id+"F7.opExtrude","SWEPT_FACE",FACE,{"disambiguationData":[OSD([sQuery(id+"F6.wireOp",EDGE,"E24.MirrorCS")])]})])],"derivedFrom":makeQuery(id+"F3.opExtrude","CAP_EDGE",EDGE,{"disambiguationData":[OSD([subQ0])],"isStart":false})});}
            var Q66;
            Q66=makeQuery(id+"F7.boolean.opBoolean","INTERSECT",EDGE,{"derivedFrom":[makeQuery(id+"F3.opExtrude","SWEPT_FACE",FACE,{"disambiguationData":[OSD([sQuery(id+"F2.wireOp",EDGE,"E6.right")])]}),makeQuery(id+"F7.opExtrude","SWEPT_FACE",FACE,{"disambiguationData":[OSD([sQuery(id+"F6.wireOp",EDGE,"E32.MirrorCS")])]})]});
            var Q67;
            {var subQ0=sQuery(id+"F2.wireOp",EDGE,"E6.right");var subQ1=sQuery(id+"F2.wireOp",EDGE,"E6.top");Q67=makeQuery(id+"F7.boolean.opBoolean","SPLIT",EDGE,{"disambiguationData":[TD([makeQuery(id+"F3.opExtrude","SWEPT_FACE",FACE,{"disambiguationData":[OSD([subQ1])]})])],"derivedFrom":makeQuery(id+"F3.opExtrude","CAP_EDGE",EDGE,{"disambiguationData":[OSD([subQ0])],"isStart":false})});}
            var Q68;
            {var subQ0=sQuery(id+"F2.wireOp",EDGE,"E6.left");var subQ1=sQuery(id+"F2.wireOp",EDGE,"E6.top");Q68=makeQuery(id+"F7.boolean.opBoolean","SPLIT",EDGE,{"disambiguationData":[TD([makeQuery(id+"F3.opExtrude","SWEPT_FACE",FACE,{"disambiguationData":[OSD([subQ1])]})])],"derivedFrom":makeQuery(id+"F3.opExtrude","CAP_EDGE",EDGE,{"disambiguationData":[OSD([subQ0])],"isStart":false})});}
            var Q69;
            {var subQ0=sQuery(id+"F2.wireOp",EDGE,"E6.left");Q69=makeQuery(id+"F7.boolean.opBoolean","SPLIT",EDGE,{"disambiguationData":[TD([makeQuery(id+"F7.opExtrude","SWEPT_FACE",FACE,{"disambiguationData":[OSD([sQuery(id+"F6.wireOp",EDGE,"E24.MirrorCS")])]})])],"derivedFrom":makeQuery(id+"F3.opExtrude","CAP_EDGE",EDGE,{"disambiguationData":[OSD([subQ0])],"isStart":false})});}
            var Q70;
            Q70=makeQuery(id+"F7.boolean.opBoolean","INTERSECT",EDGE,{"derivedFrom":[makeQuery(id+"F3.opExtrude","SWEPT_FACE",FACE,{"disambiguationData":[OSD([sQuery(id+"F2.wireOp",EDGE,"E6.left")])]}),makeQuery(id+"F7.opExtrude","SWEPT_FACE",FACE,{"disambiguationData":[OSD([sQuery(id+"F6.wireOp",EDGE,"E40.MirrorCS")])]})]});
            var Q71;
            {var subQ0=sQuery(id+"F2.wireOp",EDGE,"E6.left");Q71=makeQuery(id+"F7.boolean.opBoolean","SPLIT",EDGE,{"disambiguationData":[TD([makeQuery(id+"F7.opExtrude","SWEPT_FACE",FACE,{"disambiguationData":[OSD([sQuery(id+"F6.wireOp",EDGE,"E25.MirrorCS")])]})])],"derivedFrom":makeQuery(id+"F3.opExtrude","CAP_EDGE",EDGE,{"disambiguationData":[OSD([subQ0])],"isStart":false})});}
            var Q72;
            Q72=makeQuery(id+"F7.boolean.opBoolean","INTERSECT",EDGE,{"derivedFrom":[makeQuery(id+"F3.opExtrude","SWEPT_FACE",FACE,{"disambiguationData":[OSD([sQuery(id+"F2.wireOp",EDGE,"E6.left")])]}),makeQuery(id+"F7.opExtrude","SWEPT_FACE",FACE,{"disambiguationData":[OSD([sQuery(id+"F6.wireOp",EDGE,"E41.MirrorCS")])]})]});
            var Q73;
            {var subQ0=sQuery(id+"F2.wireOp",EDGE,"E6.left");Q73=makeQuery(id+"F7.boolean.opBoolean","SPLIT",EDGE,{"disambiguationData":[TD([makeQuery(id+"F7.opExtrude","SWEPT_FACE",FACE,{"disambiguationData":[OSD([sQuery(id+"F6.wireOp",EDGE,"E22.MirrorCS")])]})])],"derivedFrom":makeQuery(id+"F3.opExtrude","CAP_EDGE",EDGE,{"disambiguationData":[OSD([subQ0])],"isStart":false})});}
            var Q74;
            Q74=makeQuery(id+"F7.boolean.opBoolean","INTERSECT",EDGE,{"derivedFrom":[makeQuery(id+"F3.opExtrude","SWEPT_FACE",FACE,{"disambiguationData":[OSD([sQuery(id+"F2.wireOp",EDGE,"E6.left")])]}),makeQuery(id+"F7.opExtrude","SWEPT_FACE",FACE,{"disambiguationData":[OSD([sQuery(id+"F6.wireOp",EDGE,"E33.MirrorCS")])]})]});
            var Q75;
            {var subQ0=sQuery(id+"F2.wireOp",EDGE,"E6.left");Q75=makeQuery(id+"F7.boolean.opBoolean","SPLIT",EDGE,{"disambiguationData":[TD([makeQuery(id+"F7.opExtrude","SWEPT_FACE",FACE,{"disambiguationData":[OSD([sQuery(id+"F6.wireOp",EDGE,"E29.MirrorCS")])]})])],"derivedFrom":makeQuery(id+"F3.opExtrude","CAP_EDGE",EDGE,{"disambiguationData":[OSD([subQ0])],"isStart":false})});}
            var Q76;
            Q76=makeQuery(id+"F7.boolean.opBoolean","INTERSECT",EDGE,{"derivedFrom":[makeQuery(id+"F3.opExtrude","SWEPT_FACE",FACE,{"disambiguationData":[OSD([sQuery(id+"F2.wireOp",EDGE,"E6.left")])]}),makeQuery(id+"F7.opExtrude","SWEPT_FACE",FACE,{"disambiguationData":[OSD([sQuery(id+"F6.wireOp",EDGE,"E37.MirrorCS")])]})]});
            var Q77;
            {var subQ0=sQuery(id+"F2.wireOp",EDGE,"E6.bottom");var subQ1=sQuery(id+"F2.wireOp",EDGE,"E6.left");Q77=makeQuery(id+"F7.boolean.opBoolean","SPLIT",EDGE,{"disambiguationData":[TD([makeQuery(id+"F3.opExtrude","SWEPT_FACE",FACE,{"disambiguationData":[OSD([subQ0])]})])],"derivedFrom":makeQuery(id+"F3.opExtrude","CAP_EDGE",EDGE,{"disambiguationData":[OSD([subQ1])],"isStart":false})});}
            var Q78;
            Q78=makeQuery(id+"F7.boolean.opBoolean","INTERSECT",EDGE,{"derivedFrom":[makeQuery(id+"F3.opExtrude","SWEPT_FACE",FACE,{"disambiguationData":[OSD([sQuery(id+"F2.wireOp",EDGE,"E6.left")])]}),makeQuery(id+"F7.opExtrude","SWEPT_FACE",FACE,{"disambiguationData":[OSD([sQuery(id+"F6.wireOp",EDGE,"E32.MirrorCS")])]})]});
            var Q79;
            {var subQ0=sQuery(id+"F2.wireOp",EDGE,"E5.left");var subQ1=sQuery(id+"F2.wireOp",EDGE,"E5.top");Q79=makeQuery(id+"F7.boolean.opBoolean","SPLIT",EDGE,{"disambiguationData":[TD([makeQuery(id+"F3.opExtrude","SWEPT_FACE",FACE,{"disambiguationData":[OSD([subQ1])]})])],"derivedFrom":makeQuery(id+"F3.opExtrude","CAP_EDGE",EDGE,{"disambiguationData":[OSD([subQ0])],"isStart":false})});}
            var Q80;
            Q80=makeQuery(id+"F7.boolean.opBoolean","INTERSECT",EDGE,{"derivedFrom":[makeQuery(id+"F3.opExtrude","SWEPT_FACE",FACE,{"disambiguationData":[OSD([sQuery(id+"F2.wireOp",EDGE,"E5.left")])]}),makeQuery(id+"F7.opExtrude","SWEPT_FACE",FACE,{"disambiguationData":[OSD([sQuery(id+"F6.wireOp",EDGE,"E32.MirrorCS")])]})]});
            var Q81;
            {var subQ0=sQuery(id+"F2.wireOp",EDGE,"E5.left");Q81=makeQuery(id+"F7.boolean.opBoolean","SPLIT",EDGE,{"disambiguationData":[TD([makeQuery(id+"F7.opExtrude","SWEPT_FACE",FACE,{"disambiguationData":[OSD([sQuery(id+"F6.wireOp",EDGE,"E24.MirrorCS")])]})])],"derivedFrom":makeQuery(id+"F3.opExtrude","CAP_EDGE",EDGE,{"disambiguationData":[OSD([subQ0])],"isStart":false})});}
            var Q82;
            Q82=makeQuery(id+"F7.boolean.opBoolean","INTERSECT",EDGE,{"derivedFrom":[makeQuery(id+"F3.opExtrude","SWEPT_FACE",FACE,{"disambiguationData":[OSD([sQuery(id+"F2.wireOp",EDGE,"E5.left")])]}),makeQuery(id+"F7.opExtrude","SWEPT_FACE",FACE,{"disambiguationData":[OSD([sQuery(id+"F6.wireOp",EDGE,"E40.MirrorCS")])]})]});
            var Q83;
            {var subQ0=sQuery(id+"F2.wireOp",EDGE,"E5.left");Q83=makeQuery(id+"F7.boolean.opBoolean","SPLIT",EDGE,{"disambiguationData":[TD([makeQuery(id+"F7.opExtrude","SWEPT_FACE",FACE,{"disambiguationData":[OSD([sQuery(id+"F6.wireOp",EDGE,"E25.MirrorCS")])]})])],"derivedFrom":makeQuery(id+"F3.opExtrude","CAP_EDGE",EDGE,{"disambiguationData":[OSD([subQ0])],"isStart":false})});}
            var Q84;
            Q84=makeQuery(id+"F7.boolean.opBoolean","INTERSECT",EDGE,{"derivedFrom":[makeQuery(id+"F3.opExtrude","SWEPT_FACE",FACE,{"disambiguationData":[OSD([sQuery(id+"F2.wireOp",EDGE,"E5.left")])]}),makeQuery(id+"F7.opExtrude","SWEPT_FACE",FACE,{"disambiguationData":[OSD([sQuery(id+"F6.wireOp",EDGE,"E41.MirrorCS")])]})]});
            var Q85;
            {var subQ0=sQuery(id+"F2.wireOp",EDGE,"E5.left");Q85=makeQuery(id+"F7.boolean.opBoolean","SPLIT",EDGE,{"disambiguationData":[TD([makeQuery(id+"F7.opExtrude","SWEPT_FACE",FACE,{"disambiguationData":[OSD([sQuery(id+"F6.wireOp",EDGE,"E22.MirrorCS")])]})])],"derivedFrom":makeQuery(id+"F3.opExtrude","CAP_EDGE",EDGE,{"disambiguationData":[OSD([subQ0])],"isStart":false})});}
            var Q86;
            Q86=makeQuery(id+"F7.boolean.opBoolean","INTERSECT",EDGE,{"derivedFrom":[makeQuery(id+"F3.opExtrude","SWEPT_FACE",FACE,{"disambiguationData":[OSD([sQuery(id+"F2.wireOp",EDGE,"E5.left")])]}),makeQuery(id+"F7.opExtrude","SWEPT_FACE",FACE,{"disambiguationData":[OSD([sQuery(id+"F6.wireOp",EDGE,"E33.MirrorCS")])]})]});
            var Q87;
            {var subQ0=sQuery(id+"F2.wireOp",EDGE,"E5.left");Q87=makeQuery(id+"F7.boolean.opBoolean","SPLIT",EDGE,{"disambiguationData":[TD([makeQuery(id+"F7.opExtrude","SWEPT_FACE",FACE,{"disambiguationData":[OSD([sQuery(id+"F6.wireOp",EDGE,"E29.MirrorCS")])]})])],"derivedFrom":makeQuery(id+"F3.opExtrude","CAP_EDGE",EDGE,{"disambiguationData":[OSD([subQ0])],"isStart":false})});}
            var Q88;
            Q88=makeQuery(id+"F7.boolean.opBoolean","INTERSECT",EDGE,{"derivedFrom":[makeQuery(id+"F3.opExtrude","SWEPT_FACE",FACE,{"disambiguationData":[OSD([sQuery(id+"F2.wireOp",EDGE,"E5.left")])]}),makeQuery(id+"F7.opExtrude","SWEPT_FACE",FACE,{"disambiguationData":[OSD([sQuery(id+"F6.wireOp",EDGE,"E37.MirrorCS")])]})]});
            var Q89;
            {var subQ0=sQuery(id+"F2.wireOp",EDGE,"E5.bottom");var subQ1=sQuery(id+"F2.wireOp",EDGE,"E5.left");Q89=makeQuery(id+"F7.boolean.opBoolean","SPLIT",EDGE,{"disambiguationData":[TD([makeQuery(id+"F3.opExtrude","SWEPT_FACE",FACE,{"disambiguationData":[OSD([subQ0])]})])],"derivedFrom":makeQuery(id+"F3.opExtrude","CAP_EDGE",EDGE,{"disambiguationData":[OSD([subQ1])],"isStart":false})});}
            var Q90;
            {var subQ0=sQuery(id+"F2.wireOp",EDGE,"E5.bottom");var subQ1=sQuery(id+"F2.wireOp",EDGE,"E5.right");Q90=makeQuery(id+"F7.boolean.opBoolean","SPLIT",EDGE,{"disambiguationData":[TD([makeQuery(id+"F3.opExtrude","SWEPT_FACE",FACE,{"disambiguationData":[OSD([subQ0])]})])],"derivedFrom":makeQuery(id+"F3.opExtrude","CAP_EDGE",EDGE,{"disambiguationData":[OSD([subQ1])],"isStart":false})});}
            var Q91;
            Q91=makeQuery(id+"F9.boolean.opBoolean","INTERSECT",EDGE,{"derivedFrom":[makeQuery(id+"F7.boolean.opBoolean","COPY",FACE,{"disambiguationData":[TD([makeQuery(id+"F3.opExtrude","SWEPT_FACE",FACE,{"disambiguationData":[OSD([sQuery(id+"F2.wireOp",EDGE,"E5.left")])]})])],"derivedFrom":makeQuery(id+"F7.opExtrude","SWEPT_FACE",FACE,{"disambiguationData":[OSD([sQuery(id+"F6.wireOp",EDGE,"E37.MirrorCS")])]})}),makeQuery(id+"F9.opExtrude","SWEPT_FACE",FACE,{"disambiguationData":[OSD([sQuery(id+"F8.wireOp",EDGE,"E42.left")])]})]});
            var Q92;
            {var subQ0=sQuery(id+"F2.wireOp",EDGE,"E5.right");Q92=makeQuery(id+"F7.boolean.opBoolean","SPLIT",EDGE,{"disambiguationData":[TD([makeQuery(id+"F7.opExtrude","SWEPT_FACE",FACE,{"disambiguationData":[OSD([sQuery(id+"F6.wireOp",EDGE,"E29.MirrorCS")])]})])],"derivedFrom":makeQuery(id+"F3.opExtrude","CAP_EDGE",EDGE,{"disambiguationData":[OSD([subQ0])],"isStart":false})});}
            var Q93;
            Q93=makeQuery(id+"F9.boolean.opBoolean","INTERSECT",EDGE,{"derivedFrom":[makeQuery(id+"F7.boolean.opBoolean","COPY",FACE,{"disambiguationData":[TD([makeQuery(id+"F3.opExtrude","SWEPT_FACE",FACE,{"disambiguationData":[OSD([sQuery(id+"F2.wireOp",EDGE,"E5.left")])]})])],"derivedFrom":makeQuery(id+"F7.opExtrude","SWEPT_FACE",FACE,{"disambiguationData":[OSD([sQuery(id+"F6.wireOp",EDGE,"E33.MirrorCS")])]})}),makeQuery(id+"F9.opExtrude","SWEPT_FACE",FACE,{"disambiguationData":[OSD([sQuery(id+"F8.wireOp",EDGE,"E43.0.1.3")])]})]});
            var Q94;
            {var subQ0=sQuery(id+"F2.wireOp",EDGE,"E5.right");Q94=makeQuery(id+"F7.boolean.opBoolean","SPLIT",EDGE,{"disambiguationData":[TD([makeQuery(id+"F7.opExtrude","SWEPT_FACE",FACE,{"disambiguationData":[OSD([sQuery(id+"F6.wireOp",EDGE,"E22.MirrorCS")])]})])],"derivedFrom":makeQuery(id+"F3.opExtrude","CAP_EDGE",EDGE,{"disambiguationData":[OSD([subQ0])],"isStart":false})});}
            var Q95;
            Q95=makeQuery(id+"F9.boolean.opBoolean","INTERSECT",EDGE,{"derivedFrom":[makeQuery(id+"F7.boolean.opBoolean","COPY",FACE,{"disambiguationData":[TD([makeQuery(id+"F3.opExtrude","SWEPT_FACE",FACE,{"disambiguationData":[OSD([sQuery(id+"F2.wireOp",EDGE,"E5.left")])]})])],"derivedFrom":makeQuery(id+"F7.opExtrude","SWEPT_FACE",FACE,{"disambiguationData":[OSD([sQuery(id+"F6.wireOp",EDGE,"E41.MirrorCS")])]})}),makeQuery(id+"F9.opExtrude","SWEPT_FACE",FACE,{"disambiguationData":[OSD([sQuery(id+"F8.wireOp",EDGE,"E43.0.2.3")])]})]});
            var Q96;
            {var subQ0=sQuery(id+"F2.wireOp",EDGE,"E5.right");Q96=makeQuery(id+"F7.boolean.opBoolean","SPLIT",EDGE,{"disambiguationData":[TD([makeQuery(id+"F7.opExtrude","SWEPT_FACE",FACE,{"disambiguationData":[OSD([sQuery(id+"F6.wireOp",EDGE,"E25.MirrorCS")])]})])],"derivedFrom":makeQuery(id+"F3.opExtrude","CAP_EDGE",EDGE,{"disambiguationData":[OSD([subQ0])],"isStart":false})});}
            var Q97;
            Q97=makeQuery(id+"F9.boolean.opBoolean","INTERSECT",EDGE,{"derivedFrom":[makeQuery(id+"F7.boolean.opBoolean","COPY",FACE,{"disambiguationData":[TD([makeQuery(id+"F3.opExtrude","SWEPT_FACE",FACE,{"disambiguationData":[OSD([sQuery(id+"F2.wireOp",EDGE,"E5.left")])]})])],"derivedFrom":makeQuery(id+"F7.opExtrude","SWEPT_FACE",FACE,{"disambiguationData":[OSD([sQuery(id+"F6.wireOp",EDGE,"E40.MirrorCS")])]})}),makeQuery(id+"F9.opExtrude","SWEPT_FACE",FACE,{"disambiguationData":[OSD([sQuery(id+"F8.wireOp",EDGE,"E43.0.3.3")])]})]});
            var Q98;
            {var subQ0=sQuery(id+"F2.wireOp",EDGE,"E5.right");Q98=makeQuery(id+"F7.boolean.opBoolean","SPLIT",EDGE,{"disambiguationData":[TD([makeQuery(id+"F7.opExtrude","SWEPT_FACE",FACE,{"disambiguationData":[OSD([sQuery(id+"F6.wireOp",EDGE,"E24.MirrorCS")])]})])],"derivedFrom":makeQuery(id+"F3.opExtrude","CAP_EDGE",EDGE,{"disambiguationData":[OSD([subQ0])],"isStart":false})});}
            var Q99;
            Q99=makeQuery(id+"F9.boolean.opBoolean","INTERSECT",EDGE,{"derivedFrom":[makeQuery(id+"F7.boolean.opBoolean","COPY",FACE,{"disambiguationData":[TD([makeQuery(id+"F3.opExtrude","SWEPT_FACE",FACE,{"disambiguationData":[OSD([sQuery(id+"F2.wireOp",EDGE,"E5.left")])]})])],"derivedFrom":makeQuery(id+"F7.opExtrude","SWEPT_FACE",FACE,{"disambiguationData":[OSD([sQuery(id+"F6.wireOp",EDGE,"E32.MirrorCS")])]})}),makeQuery(id+"F9.opExtrude","SWEPT_FACE",FACE,{"disambiguationData":[OSD([sQuery(id+"F8.wireOp",EDGE,"E43.0.4.3")])]})]});
            var Q100;
            {var subQ0=sQuery(id+"F2.wireOp",EDGE,"E5.right");var subQ1=sQuery(id+"F2.wireOp",EDGE,"E5.top");Q100=makeQuery(id+"F7.boolean.opBoolean","SPLIT",EDGE,{"disambiguationData":[TD([makeQuery(id+"F3.opExtrude","SWEPT_FACE",FACE,{"disambiguationData":[OSD([subQ1])]})])],"derivedFrom":makeQuery(id+"F3.opExtrude","CAP_EDGE",EDGE,{"disambiguationData":[OSD([subQ0])],"isStart":false})});}
            var Q101;
            {var subQ0=sQuery(id+"F2.wireOp",EDGE,"E5.bottom");var subQ1=sQuery(id+"F2.wireOp",EDGE,"E5.right");Q101=makeQuery(id+"F7.boolean.opBoolean","SPLIT",EDGE,{"disambiguationData":[TD([makeQuery(id+"F3.opExtrude","SWEPT_FACE",FACE,{"disambiguationData":[OSD([subQ0])]})])],"derivedFrom":makeQuery(id+"F3.opExtrude","CAP_EDGE",EDGE,{"disambiguationData":[OSD([subQ1])],"isStart":true})});}
            var Q102;
            Q102=makeQuery(id+"F9.boolean.opBoolean","INTERSECT",EDGE,{"derivedFrom":[makeQuery(id+"F7.boolean.opBoolean","COPY",FACE,{"disambiguationData":[TD([makeQuery(id+"F3.opExtrude","SWEPT_FACE",FACE,{"disambiguationData":[OSD([sQuery(id+"F2.wireOp",EDGE,"E5.left")])]})])],"derivedFrom":makeQuery(id+"F7.opExtrude","SWEPT_FACE",FACE,{"disambiguationData":[OSD([sQuery(id+"F6.wireOp",EDGE,"E14.4.0.1")])]})}),makeQuery(id+"F9.opExtrude","SWEPT_FACE",FACE,{"disambiguationData":[OSD([sQuery(id+"F8.wireOp",EDGE,"E42.left")])]})]});
            var Q103;
            {var subQ0=sQuery(id+"F2.wireOp",EDGE,"E5.right");Q103=makeQuery(id+"F7.boolean.opBoolean","SPLIT",EDGE,{"disambiguationData":[TD([makeQuery(id+"F7.opExtrude","SWEPT_FACE",FACE,{"disambiguationData":[OSD([sQuery(id+"F6.wireOp",EDGE,"E14.3.0.0")])]})])],"derivedFrom":makeQuery(id+"F3.opExtrude","CAP_EDGE",EDGE,{"disambiguationData":[OSD([subQ0])],"isStart":true})});}
            var Q104;
            Q104=makeQuery(id+"F9.boolean.opBoolean","INTERSECT",EDGE,{"derivedFrom":[makeQuery(id+"F7.boolean.opBoolean","COPY",FACE,{"disambiguationData":[TD([makeQuery(id+"F3.opExtrude","SWEPT_FACE",FACE,{"disambiguationData":[OSD([sQuery(id+"F2.wireOp",EDGE,"E5.left")])]})])],"derivedFrom":makeQuery(id+"F7.opExtrude","SWEPT_FACE",FACE,{"disambiguationData":[OSD([sQuery(id+"F6.wireOp",EDGE,"E14.3.0.1")])]})}),makeQuery(id+"F9.opExtrude","SWEPT_FACE",FACE,{"disambiguationData":[OSD([sQuery(id+"F8.wireOp",EDGE,"E43.0.1.3")])]})]});
            var Q105;
            {var subQ0=sQuery(id+"F2.wireOp",EDGE,"E5.right");Q105=makeQuery(id+"F7.boolean.opBoolean","SPLIT",EDGE,{"disambiguationData":[TD([makeQuery(id+"F7.opExtrude","SWEPT_FACE",FACE,{"disambiguationData":[OSD([sQuery(id+"F6.wireOp",EDGE,"E14.2.0.0")])]})])],"derivedFrom":makeQuery(id+"F3.opExtrude","CAP_EDGE",EDGE,{"disambiguationData":[OSD([subQ0])],"isStart":true})});}
            var Q106;
            Q106=makeQuery(id+"F9.boolean.opBoolean","INTERSECT",EDGE,{"derivedFrom":[makeQuery(id+"F7.boolean.opBoolean","COPY",FACE,{"disambiguationData":[TD([makeQuery(id+"F3.opExtrude","SWEPT_FACE",FACE,{"disambiguationData":[OSD([sQuery(id+"F2.wireOp",EDGE,"E5.left")])]})])],"derivedFrom":makeQuery(id+"F7.opExtrude","SWEPT_FACE",FACE,{"disambiguationData":[OSD([sQuery(id+"F6.wireOp",EDGE,"E14.2.0.1")])]})}),makeQuery(id+"F9.opExtrude","SWEPT_FACE",FACE,{"disambiguationData":[OSD([sQuery(id+"F8.wireOp",EDGE,"E43.0.2.3")])]})]});
            var Q107;
            {var subQ0=sQuery(id+"F2.wireOp",EDGE,"E5.right");Q107=makeQuery(id+"F7.boolean.opBoolean","SPLIT",EDGE,{"disambiguationData":[TD([makeQuery(id+"F7.opExtrude","SWEPT_FACE",FACE,{"disambiguationData":[OSD([sQuery(id+"F6.wireOp",EDGE,"E14.1.0.0")])]})])],"derivedFrom":makeQuery(id+"F3.opExtrude","CAP_EDGE",EDGE,{"disambiguationData":[OSD([subQ0])],"isStart":true})});}
            var Q108;
            Q108=makeQuery(id+"F9.boolean.opBoolean","INTERSECT",EDGE,{"derivedFrom":[makeQuery(id+"F7.boolean.opBoolean","COPY",FACE,{"disambiguationData":[TD([makeQuery(id+"F3.opExtrude","SWEPT_FACE",FACE,{"disambiguationData":[OSD([sQuery(id+"F2.wireOp",EDGE,"E5.left")])]})])],"derivedFrom":makeQuery(id+"F7.opExtrude","SWEPT_FACE",FACE,{"disambiguationData":[OSD([sQuery(id+"F6.wireOp",EDGE,"E14.1.0.1")])]})}),makeQuery(id+"F9.opExtrude","SWEPT_FACE",FACE,{"disambiguationData":[OSD([sQuery(id+"F8.wireOp",EDGE,"E43.0.3.3")])]})]});
            var Q109;
            {var subQ0=sQuery(id+"F2.wireOp",EDGE,"E5.right");Q109=makeQuery(id+"F7.boolean.opBoolean","SPLIT",EDGE,{"disambiguationData":[TD([makeQuery(id+"F7.opExtrude","SWEPT_FACE",FACE,{"disambiguationData":[OSD([sQuery(id+"F6.wireOp",EDGE,"E13")])]})])],"derivedFrom":makeQuery(id+"F3.opExtrude","CAP_EDGE",EDGE,{"disambiguationData":[OSD([subQ0])],"isStart":true})});}
            var Q110;
            Q110=makeQuery(id+"F9.boolean.opBoolean","INTERSECT",EDGE,{"derivedFrom":[makeQuery(id+"F7.boolean.opBoolean","COPY",FACE,{"disambiguationData":[TD([makeQuery(id+"F3.opExtrude","SWEPT_FACE",FACE,{"disambiguationData":[OSD([sQuery(id+"F2.wireOp",EDGE,"E5.left")])]})])],"derivedFrom":makeQuery(id+"F7.opExtrude","SWEPT_FACE",FACE,{"disambiguationData":[OSD([sQuery(id+"F6.wireOp",EDGE,"E12")])]})}),makeQuery(id+"F9.opExtrude","SWEPT_FACE",FACE,{"disambiguationData":[OSD([sQuery(id+"F8.wireOp",EDGE,"E43.0.4.3")])]})]});
            var Q111;
            {var subQ0=sQuery(id+"F2.wireOp",EDGE,"E5.right");var subQ1=sQuery(id+"F2.wireOp",EDGE,"E5.top");Q111=makeQuery(id+"F7.boolean.opBoolean","SPLIT",EDGE,{"disambiguationData":[TD([makeQuery(id+"F3.opExtrude","SWEPT_FACE",FACE,{"disambiguationData":[OSD([subQ1])]})])],"derivedFrom":makeQuery(id+"F3.opExtrude","CAP_EDGE",EDGE,{"disambiguationData":[OSD([subQ0])],"isStart":true})});}
            var Q112;
            {var subQ0=sQuery(id+"F2.wireOp",EDGE,"E6.bottom");var subQ1=sQuery(id+"F2.wireOp",EDGE,"E6.left");Q112=makeQuery(id+"F7.boolean.opBoolean","SPLIT",EDGE,{"disambiguationData":[TD([makeQuery(id+"F3.opExtrude","SWEPT_FACE",FACE,{"disambiguationData":[OSD([subQ0])]})])],"derivedFrom":makeQuery(id+"F3.opExtrude","CAP_EDGE",EDGE,{"disambiguationData":[OSD([subQ1])],"isStart":true})});}
            var Q113;
            {var subQ0=sQuery(id+"F2.wireOp",EDGE,"E6.left");Q113=makeQuery(id+"F7.boolean.opBoolean","SPLIT",EDGE,{"disambiguationData":[TD([makeQuery(id+"F7.opExtrude","SWEPT_FACE",FACE,{"disambiguationData":[OSD([sQuery(id+"F6.wireOp",EDGE,"E14.3.0.0")])]})])],"derivedFrom":makeQuery(id+"F3.opExtrude","CAP_EDGE",EDGE,{"disambiguationData":[OSD([subQ0])],"isStart":true})});}
            var Q114;
            {var subQ0=sQuery(id+"F2.wireOp",EDGE,"E6.left");Q114=makeQuery(id+"F7.boolean.opBoolean","SPLIT",EDGE,{"disambiguationData":[TD([makeQuery(id+"F7.opExtrude","SWEPT_FACE",FACE,{"disambiguationData":[OSD([sQuery(id+"F6.wireOp",EDGE,"E14.2.0.0")])]})])],"derivedFrom":makeQuery(id+"F3.opExtrude","CAP_EDGE",EDGE,{"disambiguationData":[OSD([subQ0])],"isStart":true})});}
            var Q115;
            Q115=makeQuery(id+"F7.boolean.opBoolean","INTERSECT",EDGE,{"derivedFrom":[makeQuery(id+"F3.opExtrude","SWEPT_FACE",FACE,{"disambiguationData":[OSD([sQuery(id+"F2.wireOp",EDGE,"E6.left")])]}),makeQuery(id+"F7.opExtrude","SWEPT_FACE",FACE,{"disambiguationData":[OSD([sQuery(id+"F6.wireOp",EDGE,"E14.3.0.1")])]})]});
            var Q116;
            Q116=makeQuery(id+"F7.boolean.opBoolean","INTERSECT",EDGE,{"derivedFrom":[makeQuery(id+"F3.opExtrude","SWEPT_FACE",FACE,{"disambiguationData":[OSD([sQuery(id+"F2.wireOp",EDGE,"E6.left")])]}),makeQuery(id+"F7.opExtrude","SWEPT_FACE",FACE,{"disambiguationData":[OSD([sQuery(id+"F6.wireOp",EDGE,"E14.4.0.1")])]})]});
            var Q117;
            Q117=makeQuery(id+"F7.boolean.opBoolean","INTERSECT",EDGE,{"derivedFrom":[makeQuery(id+"F3.opExtrude","SWEPT_FACE",FACE,{"disambiguationData":[OSD([sQuery(id+"F2.wireOp",EDGE,"E6.left")])]}),makeQuery(id+"F7.opExtrude","SWEPT_FACE",FACE,{"disambiguationData":[OSD([sQuery(id+"F6.wireOp",EDGE,"E14.2.0.1")])]})]});
            var Q118;
            {var subQ0=sQuery(id+"F2.wireOp",EDGE,"E6.left");Q118=makeQuery(id+"F7.boolean.opBoolean","SPLIT",EDGE,{"disambiguationData":[TD([makeQuery(id+"F7.opExtrude","SWEPT_FACE",FACE,{"disambiguationData":[OSD([sQuery(id+"F6.wireOp",EDGE,"E14.1.0.0")])]})])],"derivedFrom":makeQuery(id+"F3.opExtrude","CAP_EDGE",EDGE,{"disambiguationData":[OSD([subQ0])],"isStart":true})});}
            var Q119;
            Q119=makeQuery(id+"F7.boolean.opBoolean","INTERSECT",EDGE,{"derivedFrom":[makeQuery(id+"F3.opExtrude","SWEPT_FACE",FACE,{"disambiguationData":[OSD([sQuery(id+"F2.wireOp",EDGE,"E6.left")])]}),makeQuery(id+"F7.opExtrude","SWEPT_FACE",FACE,{"disambiguationData":[OSD([sQuery(id+"F6.wireOp",EDGE,"E14.1.0.1")])]})]});
            var Q120;
            {var subQ0=sQuery(id+"F2.wireOp",EDGE,"E6.left");Q120=makeQuery(id+"F7.boolean.opBoolean","SPLIT",EDGE,{"disambiguationData":[TD([makeQuery(id+"F7.opExtrude","SWEPT_FACE",FACE,{"disambiguationData":[OSD([sQuery(id+"F6.wireOp",EDGE,"E13")])]})])],"derivedFrom":makeQuery(id+"F3.opExtrude","CAP_EDGE",EDGE,{"disambiguationData":[OSD([subQ0])],"isStart":true})});}
            var Q121;
            Q121=makeQuery(id+"F7.boolean.opBoolean","INTERSECT",EDGE,{"derivedFrom":[makeQuery(id+"F3.opExtrude","SWEPT_FACE",FACE,{"disambiguationData":[OSD([sQuery(id+"F2.wireOp",EDGE,"E6.left")])]}),makeQuery(id+"F7.opExtrude","SWEPT_FACE",FACE,{"disambiguationData":[OSD([sQuery(id+"F6.wireOp",EDGE,"E12")])]})]});
            var Q122;
            {var subQ0=sQuery(id+"F2.wireOp",EDGE,"E6.left");var subQ1=sQuery(id+"F2.wireOp",EDGE,"E6.top");Q122=makeQuery(id+"F7.boolean.opBoolean","SPLIT",EDGE,{"disambiguationData":[TD([makeQuery(id+"F3.opExtrude","SWEPT_FACE",FACE,{"disambiguationData":[OSD([subQ1])]})])],"derivedFrom":makeQuery(id+"F3.opExtrude","CAP_EDGE",EDGE,{"disambiguationData":[OSD([subQ0])],"isStart":true})});}
            var Q123;
            Q123=makeQuery(id+"F1.opExtrude","SWEPT_EDGE",EDGE,{"disambiguationData":[OSD([sQuery(id+"F0.wireOp",EDGE,"E0.bottom"),sQuery(id+"F0.wireOp",EDGE,"E0.right")])]});
            var Q124;
            {var subQ0=sQuery(id+"F2.wireOp",EDGE,"E5.bottom");var subQ1=sQuery(id+"F2.wireOp",EDGE,"E5.left");Q124=makeQuery(id+"F7.boolean.opBoolean","SPLIT",EDGE,{"disambiguationData":[TD([makeQuery(id+"F3.opExtrude","SWEPT_FACE",FACE,{"disambiguationData":[OSD([subQ0])]})])],"derivedFrom":makeQuery(id+"F3.opExtrude","CAP_EDGE",EDGE,{"disambiguationData":[OSD([subQ1])],"isStart":true})});}
            var Q125;
            {var subQ0=sQuery(id+"F2.wireOp",EDGE,"E5.left");Q125=makeQuery(id+"F7.boolean.opBoolean","SPLIT",EDGE,{"disambiguationData":[TD([makeQuery(id+"F7.opExtrude","SWEPT_FACE",FACE,{"disambiguationData":[OSD([sQuery(id+"F6.wireOp",EDGE,"E14.3.0.0")])]})])],"derivedFrom":makeQuery(id+"F3.opExtrude","CAP_EDGE",EDGE,{"disambiguationData":[OSD([subQ0])],"isStart":true})});}
            var Q126;
            {var subQ0=sQuery(id+"F2.wireOp",EDGE,"E5.left");Q126=makeQuery(id+"F7.boolean.opBoolean","SPLIT",EDGE,{"disambiguationData":[TD([makeQuery(id+"F7.opExtrude","SWEPT_FACE",FACE,{"disambiguationData":[OSD([sQuery(id+"F6.wireOp",EDGE,"E14.2.0.0")])]})])],"derivedFrom":makeQuery(id+"F3.opExtrude","CAP_EDGE",EDGE,{"disambiguationData":[OSD([subQ0])],"isStart":true})});}
            var Q127;
            {var subQ0=sQuery(id+"F2.wireOp",EDGE,"E5.left");Q127=makeQuery(id+"F7.boolean.opBoolean","SPLIT",EDGE,{"disambiguationData":[TD([makeQuery(id+"F7.opExtrude","SWEPT_FACE",FACE,{"disambiguationData":[OSD([sQuery(id+"F6.wireOp",EDGE,"E14.1.0.0")])]})])],"derivedFrom":makeQuery(id+"F3.opExtrude","CAP_EDGE",EDGE,{"disambiguationData":[OSD([subQ0])],"isStart":true})});}
            var Q128;
            {var subQ0=sQuery(id+"F2.wireOp",EDGE,"E5.left");Q128=makeQuery(id+"F7.boolean.opBoolean","SPLIT",EDGE,{"disambiguationData":[TD([makeQuery(id+"F7.opExtrude","SWEPT_FACE",FACE,{"disambiguationData":[OSD([sQuery(id+"F6.wireOp",EDGE,"E13")])]})])],"derivedFrom":makeQuery(id+"F3.opExtrude","CAP_EDGE",EDGE,{"disambiguationData":[OSD([subQ0])],"isStart":true})});}
            var Q129;
            {var subQ0=sQuery(id+"F2.wireOp",EDGE,"E5.left");var subQ1=sQuery(id+"F2.wireOp",EDGE,"E5.top");Q129=makeQuery(id+"F7.boolean.opBoolean","SPLIT",EDGE,{"disambiguationData":[TD([makeQuery(id+"F3.opExtrude","SWEPT_FACE",FACE,{"disambiguationData":[OSD([subQ1])]})])],"derivedFrom":makeQuery(id+"F3.opExtrude","CAP_EDGE",EDGE,{"disambiguationData":[OSD([subQ0])],"isStart":true})});}
            var Q130;
            Q130=makeQuery(id+"F1.opExtrude","SWEPT_EDGE",EDGE,{"disambiguationData":[OSD([sQuery(id+"F0.wireOp",EDGE,"E0.bottom"),sQuery(id+"F0.wireOp",EDGE,"E0.left")])]});
            var Q131;
            Q131=makeQuery(id+"F7.boolean.opBoolean","INTERSECT",EDGE,{"derivedFrom":[makeQuery(id+"F3.opExtrude","SWEPT_FACE",FACE,{"disambiguationData":[OSD([sQuery(id+"F2.wireOp",EDGE,"E5.left")])]}),makeQuery(id+"F7.opExtrude","SWEPT_FACE",FACE,{"disambiguationData":[OSD([sQuery(id+"F6.wireOp",EDGE,"E12")])]})]});
            var Q132;
            Q132=makeQuery(id+"F7.boolean.opBoolean","INTERSECT",EDGE,{"derivedFrom":[makeQuery(id+"F3.opExtrude","SWEPT_FACE",FACE,{"disambiguationData":[OSD([sQuery(id+"F2.wireOp",EDGE,"E5.left")])]}),makeQuery(id+"F7.opExtrude","SWEPT_FACE",FACE,{"disambiguationData":[OSD([sQuery(id+"F6.wireOp",EDGE,"E14.1.0.1")])]})]});
            var Q133;
            Q133=makeQuery(id+"F7.boolean.opBoolean","INTERSECT",EDGE,{"derivedFrom":[makeQuery(id+"F3.opExtrude","SWEPT_FACE",FACE,{"disambiguationData":[OSD([sQuery(id+"F2.wireOp",EDGE,"E5.left")])]}),makeQuery(id+"F7.opExtrude","SWEPT_FACE",FACE,{"disambiguationData":[OSD([sQuery(id+"F6.wireOp",EDGE,"E14.2.0.1")])]})]});
            var Q134;
            Q134=makeQuery(id+"F7.boolean.opBoolean","INTERSECT",EDGE,{"derivedFrom":[makeQuery(id+"F3.opExtrude","SWEPT_FACE",FACE,{"disambiguationData":[OSD([sQuery(id+"F2.wireOp",EDGE,"E5.left")])]}),makeQuery(id+"F7.opExtrude","SWEPT_FACE",FACE,{"disambiguationData":[OSD([sQuery(id+"F6.wireOp",EDGE,"E14.3.0.1")])]})]});
            var Q135;
            Q135=makeQuery(id+"F7.boolean.opBoolean","INTERSECT",EDGE,{"derivedFrom":[makeQuery(id+"F3.opExtrude","SWEPT_FACE",FACE,{"disambiguationData":[OSD([sQuery(id+"F2.wireOp",EDGE,"E5.left")])]}),makeQuery(id+"F7.opExtrude","SWEPT_FACE",FACE,{"disambiguationData":[OSD([sQuery(id+"F6.wireOp",EDGE,"E14.4.0.1")])]})]});
            fillet(context, id + "F13", {"entities" : qUnion([Q0, Q1, Q2, Q3, Q4, Q5, Q6, Q7, Q8, Q9, Q10, Q11, Q12, Q13, Q14, Q15, Q16, Q17, Q18, Q19, Q20, Q21, Q22, Q23, Q24, Q25, Q26, Q27, Q28, Q29, Q30, Q31, Q32, Q33, Q34, Q35, Q36, Q37, Q38, Q39, Q40, Q41, Q42, Q43, Q44, Q45, Q46, Q47, Q48, Q49, Q50, Q51, Q52, Q53, Q54, Q55, Q56, Q57, Q58, Q59, Q60, Q61, Q62, Q63, Q64, Q65, Q66, Q67, Q68, Q69, Q70, Q71, Q72, Q73, Q74, Q75, Q76, Q77, Q78, Q79, Q80, Q81, Q82, Q83, Q84, Q85, Q86, Q87, Q88, Q89, Q90, Q91, Q92, Q93, Q94, Q95, Q96, Q97, Q98, Q99, Q100, Q101, Q102, Q103, Q104, Q105, Q106, Q107, Q108, Q109, Q110, Q111, Q112, Q113, Q114, Q115, Q116, Q117, Q118, Q119, Q120, Q121, Q122, Q123, Q124, Q125, Q126, Q127, Q128, Q129, Q130, Q131, Q132, Q133, Q134, Q135]), "radius" : 2 * mm, "tangentPropagation" : true, "allowEdgeOverflow" : false});
        }
    });
